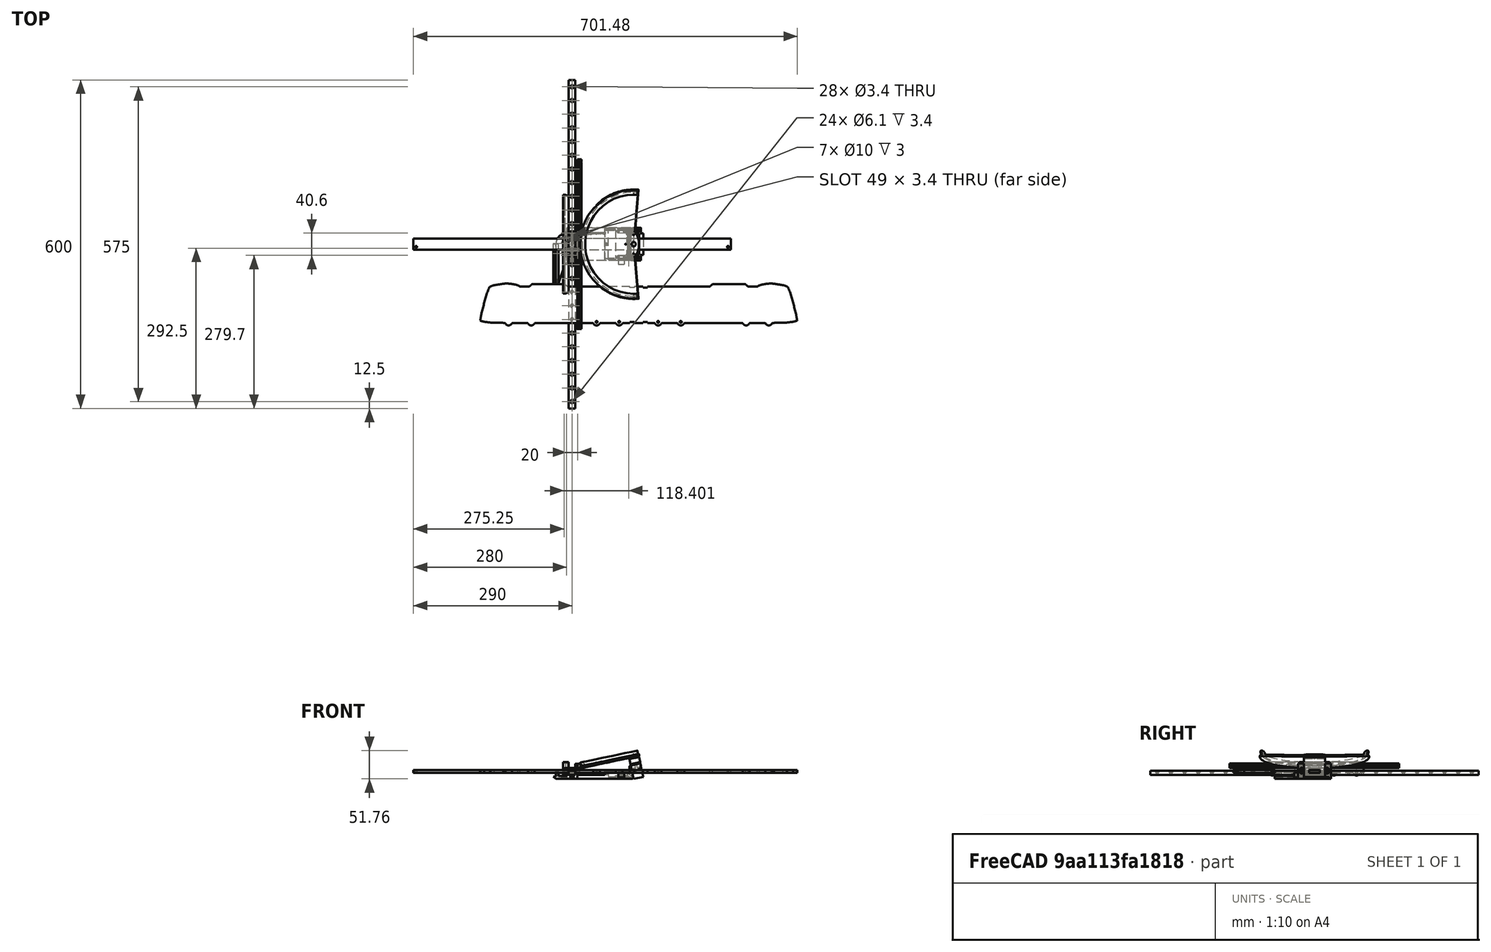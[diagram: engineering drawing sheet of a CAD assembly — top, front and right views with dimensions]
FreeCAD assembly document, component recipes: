
FREECAD ASSEMBLY — COMPONENT RECIPES ("mechanism")

This assembly document has 15 components, labeled P0..P14 below (a component is one placed body or linked part). 14 of them carry a construction recipe — the FreeCAD feature program that regenerates the part from scratch, quoted from this document or its linked companion documents; the rest are supplied as boundary geometry only. No exploded tour is included for this assembly.
NOTE — document 2 of 2 of this assembly tour. The two overview renders and the header above are repeated from document 1; the component sections below continue where the previous document stopped.
COMPONENT P12 — recipe-attached ("Stand001", modeled in this document).
Construction recipe (the document's own serialized feature program — sketch geometry with constraints, then the solid features built on it; lengths are millimeters unless a unit is written):

FEATURE [PartDesign::SubShapeBinder] Binder012
  BindCopyOnChange = 0
  BindMode = 0
  ClaimChildren = false
  Context = -> Body006 [Binder012.]
  Fuse = false
  MakeFace = true
  OffsetFill = false
  OffsetIntersection = false
  OffsetJoinType = 0
  OffsetOpenResult = false
  PartialLoad = false
  Refine = true
  Relative = true
  Support = -> [Body002[Sketch006.]]
  _Version = 2
FEATURE [PartDesign::Pad] Pad008  label="StandFootPad"
  Direction = (0,1,0)
  Length = 60
  Length2 = 10
  Midplane = true
  Profile = -> Binder012
  Refine = true
  Suppressed = false
  Type = 0
FEATURE [PartDesign::Mirrored] Mirrored003
  BaseFeature = -> Pad008
  MirrorPlane = -> YZ_Plane006
  Originals = -> [Pad008]
  Refine = true
  Suppressed = false
  TransformMode = 0
FEATURE [PartDesign::SubShapeBinder] Binder013
  BindCopyOnChange = 0
  BindMode = 0
  ClaimChildren = false
  Context = -> Body006 [Binder013.]
  Fuse = false
  MakeFace = true
  OffsetFill = false
  OffsetIntersection = false
  OffsetJoinType = 0
  OffsetOpenResult = false
  PartialLoad = false
  Refine = true
  Relative = true
  Support = -> [Body005[Sketch019.]]
  _Version = 2
FEATURE [Sketcher::SketchObject] Sketch023  label="StandCrossSection"
  ArcFitTolerance = 1e-06
  AttachmentSupport = -> [XZ_Plane006]
  ExternalGeometry = -> [Mirrored003,Binder013]
  FullyConstrained = true
  MakeInternals = false
  MapMode = 5
  Placement = pos=(0,0,0) rot=(1,0,0;1.5708rad)
  expr: Constraints[18] = <<PinionCrossSection>>.Constraints.ServoBodyWidth
  expr: Constraints[8] = <<PinionCrossSection>>.Constraints.ServoShaftLength
  sketch-geometry (26):
    g0: LineSegment StartX=9.7 StartY=-11 StartZ=0 EndX=108.652 EndY=-11 EndZ=0
    g1: LineSegment StartX=59.8197 StartY=-4 StartZ=0 EndX=9.7 EndY=-4 EndZ=0
    g2: LineSegment StartX=9.7 StartY=-4 StartZ=0 EndX=9.7 EndY=-11 EndZ=0
    g3: LineSegment [constr] StartX=112.51 StartY=31.9532 StartZ=0 EndX=113.539 EndY=27.0602 EndZ=0
    g4: LineSegment [constr] StartX=104.732 StartY=25.2077 StartZ=0 EndX=122.347 EndY=28.9128 EndZ=0
    g5: LineSegment [constr] StartX=122.347 StartY=28.9128 StartZ=0 EndX=129.963 EndY=-7.29486 EndZ=0
    g6: LineSegment [constr] StartX=129.963 StartY=-7.29486 StartZ=0 EndX=112.348 EndY=-11 EndZ=0
    g7: LineSegment [constr] StartX=112.348 StartY=-11 StartZ=0 EndX=104.732 EndY=25.2077 EndZ=0
    g8: LineSegment [constr] StartX=106.688 StartY=15.9111 StartZ=0 EndX=124.302 EndY=19.6162 EndZ=0
    g9: LineSegment [constr] StartX=124.817 StartY=17.1698 StartZ=0 EndX=107.202 EndY=13.4646 EndZ=0
    g10: LineSegment StartX=107.202 StartY=13.4646 StartZ=0 EndX=124.817 EndY=17.1698 EndZ=0
    g11: LineSegment StartX=124.817 StartY=17.1698 StartZ=0 EndX=125.64 EndY=13.2554 EndZ=0
    g12: LineSegment StartX=123.187 StartY=7.04679 StartZ=0 EndX=112.054 EndY=-0.748697 EndZ=0
    g13: LineSegment StartX=110.839 StartY=-3.82368 StartZ=0 EndX=111.587 EndY=-7.38248 EndZ=0
    g14: ArcOfCircle CenterX=108.652 CenterY=-8 CenterZ=0 NormalX=0 NormalY=0 NormalZ=1 AngleXU=0 Radius=3 StartAngle=4.71239 EndAngle=6.49051
    g15: GeomPoint [constr] X=112.348 Y=-11 Z=0
    g16: ArcOfCircle CenterX=113.774 CenterY=-3.20615 CenterZ=0 NormalX=0 NormalY=0 NormalZ=1 AngleXU=0 Radius=3 StartAngle=2.18166 EndAngle=3.34892
    g17: GeomPoint [constr] X=110.431 Y=-1.88501 Z=0
    g18: ArcOfCircle CenterX=119.713 CenterY=12.0086 CenterZ=0 NormalX=0 NormalY=0 NormalZ=1 AngleXU=0 Radius=6.05726 StartAngle=5.32325 EndAngle=6.49051
    g19: GeomPoint [constr] X=126.463 Y=9.3411 Z=0
    g20: ArcOfCircle CenterX=107.82 CenterY=10.5289 CenterZ=0 NormalX=0 NormalY=0 NormalZ=1 AngleXU=0 Radius=3 StartAngle=1.77812 EndAngle=3.14159
    g21: LineSegment StartX=104.82 StartY=4 StartZ=0 EndX=61.8197 EndY=4 EndZ=0
    g22: LineSegment StartX=59.8197 StartY=-4 StartZ=0 EndX=59.8197 EndY=2 EndZ=0
    g23: ArcOfCircle CenterX=61.8197 CenterY=2 CenterZ=0 NormalX=0 NormalY=0 NormalZ=1 AngleXU=0 Radius=2 StartAngle=1.5708 EndAngle=3.14159
    g24: GeomPoint [constr] X=59.8197 Y=4 Z=0
    g25: LineSegment StartX=104.82 StartY=10.5289 StartZ=0 EndX=104.82 EndY=4 EndZ=0
  constraints (65):
    c: Coincident(g1,g2)
    c: Coincident(g2,g0)
    c: Horizontal(g0)
    c: Horizontal(g1)
    c: Coincident(g0,g-3)
    c: Coincident(g-3,g1)
    c: Coincident(g3,g-4)
    c: PointOnObject(g-4,g3)
    c: Distance(g3,g3) = 5
    c: Coincident(g4,g5)
    c: Coincident(g5,g6)
    c: Coincident(g6,g7)
    c: Coincident(g7,g4)
    c: Perpendicular(g4,g7)
    c: Perpendicular(g5,g4)
    c: Perpendicular(g6,g5)
    c: Parallel(g3,g7)
    c: Symmetric(g4,g4,g3)
    c: Distance(g6,g6) = 18
    c: PointOnObject(g8,g7)
    c: PointOnObject(g8,g5)
    c: PointOnObject(g9,g5)
    c: PointOnObject(g9,g7)
    c: Perpendicular(g8,g7)
    c: Perpendicular(g7,g9)
    c: Distance(g8,g9) = 2.5  'ServoFlangeThickness'
    c: Distance(g9,g5) = 25  'ServoUnderFlangeHeight'
    c: Coincident(g15,g6)
    c: Coincident(g10,g9)
    c: Coincident(g11,g9)
    c: PointOnObject(g19,g5)
    c: PointOnObject(g17,g7)
    c: Distance(g11,g19) = 8
    c: PointOnObject(g15,g0)
    c: PointOnObject(g15,g13)
    c: Tangent(g0,g14) = -1.5708
    c: Tangent(g13,g14) = 1.5708
    c: Radius(g14) = 3
    c: PointOnObject(g17,g13)
    c: PointOnObject(g17,g12)
    c: Tangent(g13,g16) = -1.5708
    c: Tangent(g12,g16) = -1.5708
    c: Radius(g16) = 3
    c: PointOnObject(g19,g12)
    c: Tangent(g11,g18) = 1.5708
    c: Tangent(g12,g18) = 1.5708
    c: Symmetric(g9,g19,g11)
    c: Horizontal(g21)
    c: Coincident(g22,g1)
    c: Vertical(g22)
    c: Coincident(g10,g9)
    c: Tangent(g20,g10) = 1.5708
    c: PointOnObject(g24,g22)
    c: PointOnObject(g24,g21)
    c: Tangent(g22,g23) = 1.5708
    c: Tangent(g21,g23) = -1.5708
    c: Radius(g23) = 2
    c: Distance(g24,g0) = 15
    c: Radius(g20) = 3
    c: Coincident(g25,g20)
    c: Coincident(g25,g21)
    c: Vertical(g25)
    c: DistanceX(g24,g21) = 45
    c: Horizontal(g20,g20)
    c: Angle(g12,g25) = 0.959931
FEATURE [PartDesign::Pad] Pad009
  BaseFeature = -> Mirrored003
  Direction = (0,-1,2e-16)
  Length = 60
  Length2 = 10
  Midplane = true
  Profile = -> Sketch023
  ReferenceAxis = -> Sketch023 [N_Axis]
  Refine = true
  Suppressed = false
  Type = 0
  expr: Length = <<StandFootPad>>.Length
FEATURE [Sketcher::SketchObject] Sketch024  label="ServoCutout"
  ArcFitTolerance = 1e-06
  AttachmentSupport = -> [Pad009]
  ExternalGeometry = -> [Pad009]
  FullyConstrained = true
  MakeInternals = false
  MapMode = 5
  Placement = pos=(1.83,-2e-15,-8.69996) rot=(0,-1,0;0.207323rad)
  sketch-geometry (4):
    g0: LineSegment StartX=107.678 StartY=19.5 StartZ=0 EndX=107.678 EndY=-19.5 EndZ=0
    g1: LineSegment StartX=107.678 StartY=-19.5 StartZ=0 EndX=125.678 EndY=-19.5 EndZ=0
    g2: LineSegment StartX=125.678 StartY=-19.5 StartZ=0 EndX=125.678 EndY=19.5 EndZ=0
    g3: LineSegment StartX=125.678 StartY=19.5 StartZ=0 EndX=107.678 EndY=19.5 EndZ=0
  constraints (11):
    c: Coincident(g0,g1)
    c: Coincident(g1,g2)
    c: Coincident(g2,g3)
    c: Coincident(g3,g0)
    c: Vertical(g0)
    c: Horizontal(g1)
    c: Horizontal(g3)
    c: PointOnObject(g0,g-3)
    c: PointOnObject(g1,g-4)
    c: DistanceY(g2,g2) = 39  'ServoDepth'
    c: Symmetric(g2,g1,g-1)
FEATURE [PartDesign::Pocket] Pocket006
  BaseFeature = -> Pad009
  Direction = (0.205841,0,-0.978585)
  Length = 5
  Length2 = 5
  Profile = -> Sketch024
  ReferenceAxis = -> Sketch024 [N_Axis]
  Refine = true
  Suppressed = false
  Type = 1
FEATURE [Sketcher::SketchObject] Sketch025
  ArcFitTolerance = 1e-06
  AttachmentSupport = -> [Pad009]
  ExternalGeometry = -> [Pad009]
  FullyConstrained = true
  MakeInternals = false
  MapMode = 5
  Placement = pos=(1.83,-2e-15,-8.69996) rot=(0,-1,0;0.207323rad)
  sketch-geometry (5):
    g0: LineSegment [constr] StartX=116.678 StartY=30 StartZ=0 EndX=116.678 EndY=-30 EndZ=0
    g1: Circle CenterX=111.678 CenterY=23.5 CenterZ=0 NormalX=0 NormalY=0 NormalZ=1 AngleXU=0 Radius=1.5
    g2: Circle CenterX=121.678 CenterY=23.5 CenterZ=0 NormalX=0 NormalY=0 NormalZ=1 AngleXU=0 Radius=1.5
    g3: Circle CenterX=111.678 CenterY=-23.5 CenterZ=0 NormalX=0 NormalY=0 NormalZ=1 AngleXU=0 Radius=1.5
    g4: Circle CenterX=121.678 CenterY=-23.5 CenterZ=0 NormalX=0 NormalY=0 NormalZ=1 AngleXU=0 Radius=1.5
  constraints (12):
    c: Vertical(g0)
    c: Symmetric(g-3,g-4,g0)
    c: Symmetric(g1,g2,g0)
    c: Symmetric(g3,g4,g0)
    c: Symmetric(g3,g1,g-1)
    c: DistanceY(g4,g2) = 47
    c: DistanceX(g1,g2) = 10
    c: Equal(g1,g2)
    c: Equal(g2,g4)
    c: Equal(g4,g3)
    c: Diameter(g1) = 3
    c: Horizontal(g0,g-4)
FEATURE [PartDesign::Hole] Hole005  label="ServoScrews"
  BaseFeature = -> Pocket006
  CustomThreadClearance = 0
  Depth = 303.612
  DepthType = 1
  Diameter = 5.5
  DrillForDepth = false
  DrillPoint = 1
  DrillPointAngle = 118
  HoleCutCountersinkAngle = 90
  HoleCutCustomValues = false
  HoleCutDepth = 6.5
  HoleCutDiameter = 6.5
  HoleCutType = 1
  ModelThread = false
  Profile = -> Sketch025
  Refine = true
  Suppressed = false
  Tapered = false
  TaperedAngle = 90
  ThreadClass = 0
  ThreadDepth = 303.612
  ThreadDepthType = 0
  ThreadDirection = 0
  ThreadFit = 0
  ThreadSize = 13
  ThreadType = 1
  Threaded = false
  UseCustomThreadClearance = false
FEATURE [Sketcher::SketchObject] Sketch026
  ArcFitTolerance = 1e-06
  AttachmentSupport = -> [XY_Plane006]
  FullyConstrained = true
  MakeInternals = false
  MapMode = 5
  sketch-geometry (1):
    g0: Circle CenterX=0 CenterY=0 CenterZ=0 NormalX=0 NormalY=0 NormalZ=1 AngleXU=0 Radius=1.5
  constraints (2):
    c: Diameter(g0) = 3
    c: Coincident(g0,g-1)
FEATURE [PartDesign::Hole] Hole006  label="Rail Screw"
  BaseFeature = -> Hole005
  CustomThreadClearance = 0
  Depth = 303.612
  DepthType = 1
  Diameter = 4.4
  DrillForDepth = false
  DrillPoint = 1
  DrillPointAngle = 118
  HoleCutCountersinkAngle = 90
  HoleCutCustomValues = false
  HoleCutDepth = 0
  HoleCutDiameter = 6.1
  HoleCutType = 0
  ModelThread = false
  Profile = -> Sketch026
  Refine = true
  Suppressed = false
  Tapered = false
  TaperedAngle = 90
  ThreadClass = 0
  ThreadDepth = 303.612
  ThreadDepthType = 0
  ThreadDirection = 0
  ThreadFit = 0
  ThreadSize = 0
  ThreadType = 0
  Threaded = false
  UseCustomThreadClearance = false
FEATURE [Sketcher::SketchObject] Sketch027
  ArcFitTolerance = 1e-06
  AttachmentSupport = -> [Hole006]
  ExternalGeometry = -> [Hole006]
  FullyConstrained = true
  MakeInternals = false
  MapMode = 5
  Placement = pos=(0,0,-11) rot=(1,0,0;3.14159rad)
  expr: Constraints[23] = <<FootPads>>.Constraints.FootDiameter
  sketch-geometry (11):
    g0: LineSegment [constr] StartX=0 StartY=20.3 StartZ=0 EndX=0 EndY=-20.3 EndZ=0
    g1: LineSegment [constr] StartX=0 StartY=-20.3 StartZ=0 EndX=103.652 EndY=-20.3 EndZ=0
    g2: LineSegment [constr] StartX=103.652 StartY=-20.3 StartZ=0 EndX=103.652 EndY=20.3 EndZ=0
    g3: LineSegment [constr] StartX=103.652 StartY=20.3 StartZ=0 EndX=0 EndY=20.3 EndZ=0
    g4: LineSegment [constr] StartX=0 StartY=20.3 StartZ=0 EndX=-9.7 EndY=20.3 EndZ=0
    g5: LineSegment [constr] StartX=0 StartY=20.3 StartZ=0 EndX=0 EndY=30 EndZ=0
    g6: Circle CenterX=0 CenterY=20.3 CenterZ=0 NormalX=0 NormalY=0 NormalZ=1 AngleXU=0 Radius=5
    g7: Circle CenterX=103.652 CenterY=20.3 CenterZ=0 NormalX=0 NormalY=0 NormalZ=1 AngleXU=0 Radius=5
    g8: Circle CenterX=103.652 CenterY=-20.3 CenterZ=0 NormalX=0 NormalY=0 NormalZ=1 AngleXU=0 Radius=5
    g9: Circle CenterX=0 CenterY=-20.3 CenterZ=0 NormalX=0 NormalY=0 NormalZ=1 AngleXU=0 Radius=5
    g10: GeomPoint [constr] X=108.652 Y=20.3 Z=0
  constraints (27):
    c: Coincident(g0,g1)
    c: Coincident(g1,g2)
    c: Coincident(g2,g3)
    c: Coincident(g3,g0)
    c: Vertical(g0)
    c: Horizontal(g1)
    c: Horizontal(g3)
    c: Symmetric(g2,g1,g-1)
    c: PointOnObject(g-1,g0)
    c: Coincident(g4,g0)
    c: PointOnObject(g4,g-3)
    c: Horizontal(g4)
    c: Coincident(g5,g0)
    c: PointOnObject(g5,g-2)
    c: Horizontal(g-3,g5)
    c: Equal(g4,g5)
    c: Coincident(g6,g0)
    c: Coincident(g7,g2)
    c: Coincident(g8,g1)
    c: Coincident(g9,g0)
    c: Equal(g9,g8)
    c: Equal(g8,g7)
    c: Equal(g7,g6)
    c: Diameter(g6) = 10
    c: PointOnObject(g10,g7)
    c: Horizontal(g2,g10)
    c: PointOnObject(g10,g-4)
FEATURE [PartDesign::Pocket] Pocket007  label="FootPads001"
  BaseFeature = -> Hole006
  Direction = (0,0,1)
  Length = 3
  Length2 = 5
  Profile = -> Sketch027
  ReferenceAxis = -> Sketch027 [N_Axis]
  Refine = true
  Suppressed = false
  Type = 0
  expr: Length = <<FootPadPocket>>.Length
FEATURE [PartDesign::SubShapeBinder] Binder016
  BindCopyOnChange = 0
  BindMode = 0
  ClaimChildren = false
  Context = -> Body006 [Binder016.]
  Fuse = false
  MakeFace = true
  OffsetFill = false
  OffsetIntersection = false
  OffsetJoinType = 0
  OffsetOpenResult = false
  PartialLoad = false
  Refine = true
  Relative = true
  Support = -> [Body008[Pad016.Face4]]
  _Version = 2
FEATURE [Sketcher::SketchObject] Sketch037
  ArcFitTolerance = 1e-06
  AttachmentSupport = -> [Pocket007]
  ExternalGeometry = -> [Binder016,Pocket007]
  FullyConstrained = true
  MakeInternals = false
  MapMode = 5
  Placement = pos=(0,9e-16,4) rot=(0,0,1;0rad)
  sketch-geometry (6):
    g0: LineSegment StartX=65.8197 StartY=26 StartZ=0 EndX=65.8197 EndY=-26 EndZ=0
    g1: LineSegment StartX=65.8197 StartY=-26 StartZ=0 EndX=100.82 EndY=-26 EndZ=0
    g2: LineSegment StartX=100.82 StartY=-26 StartZ=0 EndX=100.82 EndY=26 EndZ=0
    g3: LineSegment StartX=100.82 StartY=26 StartZ=0 EndX=65.8197 EndY=26 EndZ=0
    g4: LineSegment [constr] StartX=65.8197 StartY=-26 StartZ=0 EndX=61.8197 EndY=-26 EndZ=0
    g5: LineSegment [constr] StartX=100.82 StartY=-26 StartZ=0 EndX=104.82 EndY=-26 EndZ=0
  constraints (17):
    c: Coincident(g0,g1)
    c: Coincident(g1,g2)
    c: Coincident(g2,g3)
    c: Coincident(g3,g0)
    c: Vertical(g2)
    c: Horizontal(g1)
    c: Horizontal(g3)
    c: Symmetric(g0,g0,g-1)
    c: Distance(g1,g-4) = 0.5
    c: Coincident(g4,g0)
    c: Horizontal(g4)
    c: Coincident(g5,g1)
    c: Horizontal(g5)
    c: Vertical(g5,g-6)
    c: Vertical(g4,g-5)
    c: Equal(g4,g5)
    c: Distance(g-5,g0) = 4
FEATURE [PartDesign::Pocket] Pocket011  label="ElectronicsCarveOut"
  BaseFeature = -> Pocket007
  Direction = (0,0,-1)
  Length = 0
  Length2 = 5
  Offset = 1
  Profile = -> Sketch037
  ReferenceAxis = -> Sketch037 [N_Axis]
  Refine = true
  Suppressed = false
  Type = 3
  UpToFace = -> Binder016 [Face1]
FEATURE [Sketcher::SketchObject] Sketch038
  ArcFitTolerance = 1e-06
  AttachmentSupport = -> [Pocket011]
  ExternalGeometry = -> [Binder016]
  FullyConstrained = true
  MakeInternals = false
  MapMode = 5
  Placement = pos=(0,0,-7) rot=(0,0,1;0rad)
  sketch-geometry (6):
    g0: Circle CenterX=84.3 CenterY=23.5 CenterZ=0 NormalX=0 NormalY=0 NormalZ=1 AngleXU=0 Radius=2.35
    g1: Circle CenterX=95.7 CenterY=23.5 CenterZ=0 NormalX=0 NormalY=0 NormalZ=1 AngleXU=0 Radius=2.35
    g2: Circle CenterX=84.3 CenterY=-23.5 CenterZ=0 NormalX=0 NormalY=0 NormalZ=1 AngleXU=0 Radius=2.35
    g3: Circle CenterX=95.7 CenterY=-23.5 CenterZ=0 NormalX=0 NormalY=0 NormalZ=1 AngleXU=0 Radius=2.35
    g4: GeomPoint X=84.3 Y=24.55 Z=0
    g5: GeomPoint X=84.3 Y=25.85 Z=0
  constraints (12):
    c: Coincident(g0,g-3)
    c: Coincident(g1,g-4)
    c: Coincident(g2,g-5)
    c: Coincident(g3,g-6)
    c: Equal(g2,g3)
    c: Equal(g3,g0)
    c: Equal(g0,g1)
    c: PointOnObject(g4,g-3)
    c: PointOnObject(g5,g0)
    c: Vertical(g0,g4)
    c: Vertical(g4,g5)
    c: Distance(g4,g0) = 1.3
FEATURE [PartDesign::Pad] Pad017  label="PCBStandoff"
  BaseFeature = -> Pocket011
  Direction = (0,0,1)
  Length = 10
  Length2 = 10
  Profile = -> Sketch038
  ReferenceAxis = -> Sketch038 [N_Axis]
  Refine = true
  Suppressed = false
  Type = 3
  UpToFace = -> Binder016 [Face1]
FEATURE [Sketcher::SketchObject] Sketch039
  ArcFitTolerance = 1e-06
  AttachmentSupport = -> [Pad017]
  ExternalGeometry = -> [Binder016]
  FullyConstrained = true
  MakeInternals = false
  MapMode = 5
  Placement = pos=(0,0,-6) rot=(0,0,1;0rad)
  sketch-geometry (4):
    g0: Circle CenterX=84.3 CenterY=23.5 CenterZ=0 NormalX=0 NormalY=0 NormalZ=1 AngleXU=0 Radius=1.05
    g1: Circle CenterX=95.7 CenterY=23.5 CenterZ=0 NormalX=0 NormalY=0 NormalZ=1 AngleXU=0 Radius=1.05
    g2: Circle CenterX=84.3 CenterY=-23.5 CenterZ=0 NormalX=0 NormalY=0 NormalZ=1 AngleXU=0 Radius=1.05
    g3: Circle CenterX=95.7 CenterY=-23.5 CenterZ=0 NormalX=0 NormalY=0 NormalZ=1 AngleXU=0 Radius=1.05
  constraints (8):
    c: Coincident(g0,g-3)
    c: Equal(g0,g-3)
    c: Coincident(g1,g-4)
    c: Equal(g1,g-4)
    c: Coincident(g2,g-5)
    c: Equal(g2,g-5)
    c: Coincident(g3,g-6)
    c: Equal(g3,g-6)
FEATURE [PartDesign::Hole] Hole007  label="PCBMountHoles"
  BaseFeature = -> Pad017
  CustomThreadClearance = 0
  Depth = 3.5
  DepthType = 0
  Diameter = 3
  DrillForDepth = false
  DrillPoint = 0
  DrillPointAngle = 118
  HoleCutCountersinkAngle = 90
  HoleCutCustomValues = false
  HoleCutDepth = 0
  HoleCutDiameter = 6.1
  HoleCutType = 0
  ModelThread = false
  Profile = -> Sketch039
  Refine = true
  Suppressed = false
  Tapered = false
  TaperedAngle = 90
  ThreadClass = 0
  ThreadDepth = 3.5
  ThreadDepthType = 0
  ThreadDirection = 0
  ThreadFit = 0
  ThreadSize = 0
  ThreadType = 0
  Threaded = false
  UseCustomThreadClearance = false
FEATURE [PartDesign::SubShapeBinder] Binder017
  BindCopyOnChange = 0
  BindMode = 0
  ClaimChildren = false
  Context = -> Body006 [Binder017.]
  Fuse = false
  MakeFace = true
  OffsetFill = false
  OffsetIntersection = false
  OffsetJoinType = 0
  OffsetOpenResult = false
  PartialLoad = false
  Refine = true
  Relative = true
  Support = -> [Body008[Pad016.Face14,Pad016.Face15,Pad016.Face16]]
  _Version = 2
FEATURE [Sketcher::SketchObject] Sketch040
  ArcFitTolerance = 1e-06
  AttachmentSupport = -> [Hole007]
  ExternalGeometry = -> [Binder017]
  FullyConstrained = true
  MakeInternals = false
  MapMode = 5
  Placement = pos=(0,-30,8.1e-15) rot=(1,0,0;1.5708rad)
  sketch-geometry (10):
    g0: LineSegment StartX=84.5 StartY=-0.3 StartZ=0 EndX=84.5 EndY=-7.3 EndZ=0
    g1: LineSegment StartX=85.5 StartY=-8.3 StartZ=0 EndX=94.5 EndY=-8.3 EndZ=0
    g2: LineSegment StartX=95.5 StartY=-7.3 StartZ=0 EndX=95.5 EndY=-0.3 EndZ=0
    g3: LineSegment StartX=94.5 StartY=0.7 StartZ=0 EndX=85.5 EndY=0.7 EndZ=0
    g4: ArcOfCircle CenterX=85.5 CenterY=-0.3 CenterZ=0 NormalX=0 NormalY=0 NormalZ=1 AngleXU=0 Radius=1 StartAngle=1.5708 EndAngle=3.14159
    g5: ArcOfCircle CenterX=85.5 CenterY=-7.3 CenterZ=0 NormalX=0 NormalY=0 NormalZ=1 AngleXU=0 Radius=1 StartAngle=3.14159 EndAngle=4.71239
    g6: ArcOfCircle CenterX=94.5 CenterY=-7.3 CenterZ=0 NormalX=0 NormalY=0 NormalZ=1 AngleXU=0 Radius=1 StartAngle=4.71239 EndAngle=6.28319
    g7: ArcOfCircle CenterX=94.5 CenterY=-0.3 CenterZ=0 NormalX=0 NormalY=0 NormalZ=1 AngleXU=0 Radius=1 StartAngle=0 EndAngle=1.5708
    g8: GeomPoint [constr] X=84.5 Y=0.7 Z=0
    g9: GeomPoint [constr] X=95.5 Y=-8.3 Z=0
  constraints (22):
    c: Tangent(g0,g4) = -1.5708
    c: Tangent(g0,g5) = -1.5708
    c: Tangent(g1,g5) = -1.5708
    c: Tangent(g1,g6) = -1.5708
    c: Tangent(g2,g6) = -1.5708
    c: Tangent(g2,g7) = -1.5708
    c: Tangent(g3,g7) = -1.5708
    c: Tangent(g3,g4) = -1.5708
    c: Vertical(g0)
    c: Vertical(g2)
    c: Horizontal(g1)
    c: Horizontal(g3)
    c: Equal(g4,g5)
    c: Equal(g5,g6)
    c: Equal(g6,g7)
    c: PointOnObject(g8,g0)
    c: PointOnObject(g8,g3)
    c: PointOnObject(g9,g1)
    c: PointOnObject(g9,g2)
    c: Radius(g5) = 1
    c: Coincident(g8,g-3)
    c: Coincident(g9,g-4)
FEATURE [PartDesign::Pocket] Pocket012  label="USBPlugCarve"
  BaseFeature = -> Hole007
  Direction = (0,1,-2e-16)
  Length = 0
  Length2 = 5
  Profile = -> Sketch040
  ReferenceAxis = -> Sketch040 [N_Axis]
  Refine = true
  Suppressed = false
  Type = 3
  UpToFace = -> Binder017 [Face3]
FEATURE [Sketcher::SketchObject] Sketch041
  ArcFitTolerance = 1e-06
  AttachmentSupport = -> [Pocket012]
  ExternalGeometry = -> [Binder017]
  FullyConstrained = true
  MakeInternals = false
  MapMode = 5
  Placement = pos=(0,-26.8,0) rot=(1,0,0;1.5708rad)
  sketch-geometry (12):
    g0: LineSegment [constr] StartX=86 StartY=-2.3 StartZ=0 EndX=86 EndY=-5.3 EndZ=0
    g1: LineSegment [constr] StartX=86 StartY=-5.3 StartZ=0 EndX=94 EndY=-5.3 EndZ=0
    g2: LineSegment [constr] StartX=94 StartY=-5.3 StartZ=0 EndX=94 EndY=-2.3 EndZ=0
    g3: LineSegment [constr] StartX=94 StartY=-2.3 StartZ=0 EndX=86 EndY=-2.3 EndZ=0
    g4: LineSegment StartX=94.3 StartY=-5.3 StartZ=0 EndX=94.3 EndY=-2.3 EndZ=0
    g5: ArcOfCircle CenterX=94 CenterY=-2.3 CenterZ=0 NormalX=0 NormalY=0 NormalZ=-1 AngleXU=0 Radius=0.3 StartAngle=1.5708 EndAngle=3.14159
    g6: LineSegment StartX=94 StartY=-2 StartZ=0 EndX=86 EndY=-2 EndZ=0
    g7: ArcOfCircle CenterX=86 CenterY=-2.3 CenterZ=0 NormalX=0 NormalY=0 NormalZ=-1 AngleXU=-1.5708 Radius=0.3 StartAngle=1.5708 EndAngle=3.14159
    g8: LineSegment StartX=85.7 StartY=-2.3 StartZ=0 EndX=85.7 EndY=-5.3 EndZ=0
    g9: ArcOfCircle CenterX=86 CenterY=-5.3 CenterZ=0 NormalX=0 NormalY=0 NormalZ=-1 AngleXU=-3.14159 Radius=0.3 StartAngle=1.5708 EndAngle=3.14159
    g10: LineSegment StartX=86 StartY=-5.6 StartZ=0 EndX=94 EndY=-5.6 EndZ=0
    g11: ArcOfCircle CenterX=94 CenterY=-5.3 CenterZ=0 NormalX=0 NormalY=0 NormalZ=-1 AngleXU=1.5708 Radius=0.3 StartAngle=1.5708 EndAngle=3.14159
  constraints (26):
    c: Coincident(g0,g1)
    c: Coincident(g1,g2)
    c: Coincident(g2,g3)
    c: Coincident(g3,g0)
    c: Vertical(g0)
    c: Vertical(g2)
    c: Horizontal(g1)
    c: Horizontal(g3)
    c: Coincident(g0,g-3)
    c: Coincident(g1,g-4)
    c: Tangent(g4,g5) = -1.5708
    c: Tangent(g4,g11) = -1.5708
    c: Tangent(g5,g6) = -1.5708
    c: Tangent(g6,g7) = -1.5708
    c: Tangent(g7,g8) = -1.5708
    c: Tangent(g8,g9) = -1.5708
    c: Tangent(g9,g10) = -1.5708
    c: Tangent(g10,g11) = -1.5708
    c: Coincident(g11,g1)
    c: Parallel(g4,g2)
    c: Coincident(g5,g3)
    c: Parallel(g6,g3)
    c: Coincident(g7,g3)
    c: Parallel(g8,g0)
    c: Coincident(g9,g0)
    c: Distance(g10,g1) = 0.3
FEATURE [PartDesign::Pocket] Pocket013  label="USBSocketCarve"
  BaseFeature = -> Pocket012
  Direction = (0,1,-2e-16)
  Length = 5
  Length2 = 5
  Profile = -> Sketch041
  ReferenceAxis = -> Sketch041 [N_Axis]
  Refine = true
  Suppressed = false
  Type = 2
FEATURE [Sketcher::SketchObject] Sketch042
  ArcFitTolerance = 1e-06
  AttachmentSupport = -> [Pocket013]
  ExternalGeometry = -> [Pocket013]
  FullyConstrained = true
  MakeInternals = false
  MapMode = 5
  Placement = pos=(100.82,0,0) rot=(0.57735,-0.57735,-0.57735;2.0944rad)
  sketch-geometry (4):
    g0: LineSegment StartX=-26 StartY=4 StartZ=0 EndX=-28 EndY=2 EndZ=0
    g1: LineSegment StartX=-28 StartY=2 StartZ=0 EndX=28 EndY=2 EndZ=0
    g2: LineSegment StartX=28 StartY=2 StartZ=0 EndX=26 EndY=4 EndZ=0
    g3: LineSegment StartX=26 StartY=4 StartZ=0 EndX=-26 EndY=4 EndZ=0
  constraints (11):
    c: Distance(g-6,g-3) = 2
    c: Coincident(g0,g-5)
    c: PointOnObject(g0,g-6)
    c: Coincident(g0,g1)
    c: PointOnObject(g1,g-6)
    c: Coincident(g1,g2)
    c: Coincident(g2,g-4)
    c: Coincident(g2,g3)
    c: Coincident(g3,g0)
    c: Angle(g1,g0) = 0.785398
    c: Equal(g0,g2)
FEATURE [PartDesign::Pocket] Pocket014  label="LidSlot"
  BaseFeature = -> Pocket013
  Direction = (1,0,0)
  Length = 0
  Length2 = 5
  Profile = -> Sketch042
  ReferenceAxis = -> Sketch042 [N_Axis]
  Refine = true
  Suppressed = false
  Type = 3
  UpToFace = -> Pocket013 [Face17]
FEATURE [PartDesign::Pocket] Pocket015  label="LidOvershoot"
  BaseFeature = -> Pocket014
  Direction = (1,0,0)
  Length = 2
  Length2 = 5
  Profile = -> Sketch042
  ReferenceAxis = -> Sketch042 [N_Axis]
  Refine = true
  Suppressed = false
  Type = 0
FEATURE [Sketcher::SketchObject] Sketch043
  ArcFitTolerance = 1e-06
  AttachmentSupport = -> [Pocket015]
  ExternalGeometry = -> [Pocket015]
  FullyConstrained = true
  MakeInternals = false
  MapMode = 5
  Placement = pos=(0,0,2) rot=(0,0,1;0rad)
  sketch-geometry (3):
    g0: Circle CenterX=62.8197 CenterY=-1.9806e-12 CenterZ=0 NormalX=0 NormalY=0 NormalZ=1 AngleXU=0 Radius=1.5
    g1: GeomPoint X=59.8197 Y=-3.9648e-12 Z=0
    g2: GeomPoint X=65.8197 Y=3.6e-15 Z=0
  constraints (4):
    c: Symmetric(g-4,g-4,g1)
    c: Symmetric(g-3,g-3,g2)
    c: Symmetric(g1,g2,g0)
    c: Diameter(g0) = 3
FEATURE [PartDesign::Hole] Hole008  label="LidScrewHole"
  BaseFeature = -> Pocket015
  CustomThreadClearance = 0
  Depth = 6
  DepthType = 0
  Diameter = 3
  DrillForDepth = false
  DrillPoint = 0
  DrillPointAngle = 118
  HoleCutCountersinkAngle = 90
  HoleCutCustomValues = false
  HoleCutDepth = 0
  HoleCutDiameter = 6.1
  HoleCutType = 0
  ModelThread = false
  Profile = -> Sketch043
  Refine = true
  Suppressed = false
  Tapered = false
  TaperedAngle = 90
  ThreadClass = 0
  ThreadDepth = 6
  ThreadDepthType = 0
  ThreadDirection = 0
  ThreadFit = 0
  ThreadSize = 0
  ThreadType = 0
  Threaded = false
  UseCustomThreadClearance = false
FEATURE [Sketcher::SketchObject] Sketch044  label="SocketPipeSection"
  ArcFitTolerance = 1e-06
  AttachmentSupport = -> [Hole008]
  ExternalGeometry = -> [Hole008]
  FullyConstrained = true
  MakeInternals = false
  MapMode = 5
  Placement = pos=(100.82,0,0) rot=(0.57735,-0.57735,-0.57735;2.0944rad)
  expr: Constraints[10] = 7.62 + 2
  expr: Constraints[11] = 2.54 + 2
  sketch-geometry (4):
    g0: LineSegment StartX=-26 StartY=-4.54 StartZ=0 EndX=-16.38 EndY=-4.54 EndZ=0
    g1: LineSegment StartX=-16.38 StartY=-4.54 StartZ=0 EndX=-16.38 EndY=0 EndZ=0
    g2: LineSegment StartX=-16.38 StartY=0 StartZ=0 EndX=-26 EndY=0 EndZ=0
    g3: LineSegment StartX=-26 StartY=0 StartZ=0 EndX=-26 EndY=-4.54 EndZ=0
  constraints (12):
    c: Coincident(g0,g1)
    c: Coincident(g1,g2)
    c: Coincident(g2,g3)
    c: Coincident(g3,g0)
    c: Horizontal(g0)
    c: Horizontal(g2)
    c: Vertical(g1)
    c: Vertical(g3)
    c: PointOnObject(g0,g-4)
    c: PointOnObject(g1,g-1)
    c: DistanceX(g0,g0) = 9.62
    c: Distance(g1,g1) = 4.54
FEATURE [Sketcher::SketchObject] Sketch045  label="SocketPipePath"
  ArcFitTolerance = 1e-06
  AttachmentSupport = -> [Hole008]
  ExternalGeometry = -> [Sketch044,Hole008]
  FullyConstrained = true
  MakeInternals = false
  MapMode = 5
  Placement = pos=(0,26,0) rot=(1,0,0;1.5708rad)
  sketch-geometry (2):
    g0: LineSegment StartX=100.82 StartY=-1.9e-15 StartZ=0 EndX=111.652 EndY=-7.42652 EndZ=0
    g1: GeomPoint [constr] X=111.652 Y=-8 Z=0
  constraints (5):
    c: Coincident(g0,g-3)
    c: PointOnObject(g1,g-5)
    c: Horizontal(g-5,g1)
    c: PointOnObject(g-5,g0)
    c: Vertical(g0,g1)
FEATURE [PartDesign::SubtractivePipe] SubtractivePipe  label="ServoCablePipe"
  AuxilleryCurvelinear = true
  AuxillerySpineTangent = false
  BaseFeature = -> Hole008
  Binormal = (0,0,0)
  Mode = 0
  Profile = -> Sketch044
  Refine = true
  Spine = -> Sketch045
  SpineTangent = false
  Suppressed = false
  Transformation = 0
  Transition = 0
FEATURE [Sketcher::SketchObject] Sketch049
  ArcFitTolerance = 1e-06
  AttachmentSupport = -> [XZ_Plane006]
  ExternalGeometry = -> [SubtractivePipe]
  FullyConstrained = true
  MakeInternals = false
  MapMode = 5
  Placement = pos=(0,0,0) rot=(1,0,0;1.5708rad)
  sketch-geometry (3):
    g0: LineSegment StartX=101.665 StartY=4 StartZ=0 EndX=102.82 EndY=2 EndZ=0
    g1: LineSegment StartX=102.82 StartY=2 StartZ=0 EndX=102.82 EndY=4 EndZ=0
    g2: LineSegment StartX=102.82 StartY=4 StartZ=0 EndX=101.665 EndY=4 EndZ=0
  constraints (7):
    c: Coincident(g0,g1)
    c: Coincident(g1,g2)
    c: Coincident(g2,g0)
    c: Horizontal(g2)
    c: Angle(g0,g-1) = 1.0472
    c: Coincident(g1,g-3)
    c: Coincident(g0,g-3)
FEATURE [PartDesign::Pad] Pad020  label="LidRearLip"
  BaseFeature = -> SubtractivePipe
  Direction = (0,-1,2e-16)
  Length = 10
  Length2 = 10
  Profile = -> Sketch049
  ReferenceAxis = -> Sketch049 [N_Axis]
  Refine = true
  Suppressed = false
  Type = 2
FEATURE [PartDesign::Mirrored] Mirrored004  label="LidRearLipReflection"
  BaseFeature = -> Pad020
  MirrorPlane = -> XZ_Plane006
  Originals = -> [Pad020]
  Refine = true
  Suppressed = false
  TransformMode = 0
FEATURE [Sketcher::SketchObject] Sketch065
  ArcFitTolerance = 1e-06
  FullyConstrained = false
  MakeInternals = false
  Placement = pos=(0,0,-11) rot=(0,0,-1;3.14159rad)
  sketch-geometry (193):
    g0: LineSegment StartX=-17 StartY=-18.5371 StartZ=0 EndX=-17 EndY=-21.5 EndZ=0
    g1: LineSegment StartX=-17 StartY=-21.5 StartZ=0 EndX=-17.7681 EndY=-21.5 EndZ=0
    g2: LineSegment StartX=-17.7681 StartY=-21.5 StartZ=0 EndX=-17.7681 EndY=-19.7222 EndZ=0
    g3: BSplineCurve PolesCount=4 KnotsCount=2 Degree=3 IsPeriodic=0
    g4: BSplineCurve PolesCount=4 KnotsCount=2 Degree=3 IsPeriodic=0
    g5: LineSegment StartX=-18.7119 StartY=-19.5246 StartZ=0 EndX=-18.7119 EndY=-21.5 EndZ=0
    g6: LineSegment StartX=-18.7119 StartY=-21.5 StartZ=0 EndX=-19.4801 EndY=-21.5 EndZ=0
    g7: LineSegment StartX=-19.4801 StartY=-21.5 StartZ=0 EndX=-19.4801 EndY=-19.7222 EndZ=0
    g8: BSplineCurve PolesCount=4 KnotsCount=2 Degree=3 IsPeriodic=0
    g9: BSplineCurve PolesCount=4 KnotsCount=2 Degree=3 IsPeriodic=0
    g10: LineSegment StartX=-20.424 StartY=-19.5246 StartZ=0 EndX=-20.424 EndY=-21.5 EndZ=0
    g11: LineSegment StartX=-20.424 StartY=-21.5 StartZ=0 EndX=-21.1922 EndY=-21.5 EndZ=0
    g12: LineSegment StartX=-21.1922 StartY=-21.5 StartZ=0 EndX=-21.1922 EndY=-19.4041 EndZ=0
    g13: BSplineCurve PolesCount=4 KnotsCount=2 Degree=3 IsPeriodic=0
    g14: BSplineCurve PolesCount=4 KnotsCount=2 Degree=3 IsPeriodic=0
    g15: BSplineCurve PolesCount=4 KnotsCount=2 Degree=3 IsPeriodic=0
    g16: BSplineCurve PolesCount=4 KnotsCount=2 Degree=3 IsPeriodic=0
    g17: LineSegment StartX=-17.7627 StartY=-18.9047 StartZ=0 EndX=-17.7627 EndY=-18.5371 EndZ=0
    g18: LineSegment StartX=-17.7627 StartY=-18.5371 StartZ=0 EndX=-17 EndY=-18.5371 EndZ=0
    g19: BSplineCurve PolesCount=4 KnotsCount=2 Degree=3 IsPeriodic=0
    g20: BSplineCurve PolesCount=4 KnotsCount=2 Degree=3 IsPeriodic=0
    g21: LineSegment StartX=-23.536 StartY=-21.5 StartZ=0 EndX=-24.3702 EndY=-21.5 EndZ=0
    g22: LineSegment StartX=-24.3702 StartY=-21.5 StartZ=0 EndX=-24.3702 EndY=-21.4068 EndZ=0
    g23: BSplineCurve PolesCount=4 KnotsCount=2 Degree=3 IsPeriodic=0
    g24: LineSegment StartX=-24.1946 StartY=-21.0447 StartZ=0 EndX=-24.1946 EndY=-19.3985 EndZ=0
    g25: BSplineCurve PolesCount=4 KnotsCount=2 Degree=3 IsPeriodic=0
    g26: BSplineCurve PolesCount=4 KnotsCount=2 Degree=3 IsPeriodic=0
    g27: LineSegment StartX=-21.7143 StartY=-19.5138 StartZ=0 EndX=-22.455 EndY=-19.5138 EndZ=0
    g28: BSplineCurve PolesCount=4 KnotsCount=2 Degree=3 IsPeriodic=0
    g29: BSplineCurve PolesCount=4 KnotsCount=2 Degree=3 IsPeriodic=0
    g30: BSplineCurve PolesCount=4 KnotsCount=2 Degree=3 IsPeriodic=0
    g31: LineSegment StartX=-22.8282 StartY=-19.7497 StartZ=0 EndX=-22.5209 EndY=-19.8045 EndZ=0
    g32: BSplineCurve PolesCount=4 KnotsCount=2 Degree=3 IsPeriodic=0
    g33: BSplineCurve PolesCount=4 KnotsCount=2 Degree=3 IsPeriodic=0
    g34: BSplineCurve PolesCount=4 KnotsCount=2 Degree=3 IsPeriodic=0
    g35: BSplineCurve PolesCount=4 KnotsCount=2 Degree=3 IsPeriodic=0
    g36: BSplineCurve PolesCount=4 KnotsCount=2 Degree=3 IsPeriodic=0
    g37: LineSegment StartX=-22.8557 StartY=-20.2436 StartZ=0 EndX=-23.1191 EndY=-20.1941 EndZ=0
    g38: BSplineCurve PolesCount=4 KnotsCount=2 Degree=3 IsPeriodic=0
    g39: LineSegment StartX=-23.4428 StartY=-20.1009 StartZ=0 EndX=-23.4428 EndY=-20.3093 EndZ=0
    g40: LineSegment StartX=-25.6028 StartY=-18.5371 StartZ=0 EndX=-24.8348 EndY=-18.5371 EndZ=0
    g41: LineSegment StartX=-24.8348 StartY=-18.5371 StartZ=0 EndX=-24.8348 EndY=-21.5 EndZ=0
    g42: LineSegment StartX=-24.8348 StartY=-21.5 StartZ=0 EndX=-25.6028 EndY=-21.5 EndZ=0
    g43: LineSegment StartX=-25.6028 StartY=-21.5 StartZ=0 EndX=-25.6028 EndY=-18.5371 EndZ=0
    g44: LineSegment StartX=-25.6028 StartY=-17.5 StartZ=0 EndX=-24.8348 EndY=-17.5 EndZ=0
    g45: LineSegment StartX=-24.8348 StartY=-17.5 StartZ=0 EndX=-24.8348 EndY=-18.1859 EndZ=0
    g46: LineSegment StartX=-24.8348 StartY=-18.1859 StartZ=0 EndX=-25.6028 EndY=-18.1859 EndZ=0
    g47: LineSegment StartX=-25.6028 StartY=-18.1859 StartZ=0 EndX=-25.6028 EndY=-17.5 EndZ=0
    g48: LineSegment StartX=-27.0432 StartY=-17.5 StartZ=0 EndX=-26.2752 EndY=-17.5 EndZ=0
    g49: LineSegment StartX=-26.2752 StartY=-17.5 StartZ=0 EndX=-26.2752 EndY=-21.5 EndZ=0
    g50: LineSegment StartX=-26.2752 StartY=-21.5 StartZ=0 EndX=-27.0432 EndY=-21.5 EndZ=0
    g51: LineSegment StartX=-27.0432 StartY=-21.5 StartZ=0 EndX=-27.0432 EndY=-17.5 EndZ=0
    g52: BSplineCurve PolesCount=4 KnotsCount=2 Degree=3 IsPeriodic=0
    g53: BSplineCurve PolesCount=4 KnotsCount=2 Degree=3 IsPeriodic=0
    g54: BSplineCurve PolesCount=4 KnotsCount=2 Degree=3 IsPeriodic=0
    g55: BSplineCurve PolesCount=4 KnotsCount=2 Degree=3 IsPeriodic=0
    g56: BSplineCurve PolesCount=4 KnotsCount=2 Degree=3 IsPeriodic=0
    g57: BSplineCurve PolesCount=4 KnotsCount=2 Degree=3 IsPeriodic=0
    g58: BSplineCurve PolesCount=4 KnotsCount=2 Degree=3 IsPeriodic=0
    g59: BSplineCurve PolesCount=4 KnotsCount=2 Degree=3 IsPeriodic=0
    g60: BSplineCurve PolesCount=4 KnotsCount=2 Degree=3 IsPeriodic=0
    g61: LineSegment StartX=-31.384 StartY=-22.005 StartZ=0 EndX=-31.2304 EndY=-21.6043 EndZ=0
    g62: BSplineCurve PolesCount=4 KnotsCount=2 Degree=3 IsPeriodic=0
    g63: BSplineCurve PolesCount=4 KnotsCount=2 Degree=3 IsPeriodic=0
    g64: BSplineCurve PolesCount=4 KnotsCount=2 Degree=3 IsPeriodic=0
    g65: BSplineCurve PolesCount=4 KnotsCount=2 Degree=3 IsPeriodic=0
    g66: BSplineCurve PolesCount=4 KnotsCount=2 Degree=3 IsPeriodic=0
    g67: BSplineCurve PolesCount=4 KnotsCount=2 Degree=3 IsPeriodic=0
    g68: BSplineCurve PolesCount=4 KnotsCount=2 Degree=3 IsPeriodic=0
    g69: BSplineCurve PolesCount=4 KnotsCount=2 Degree=3 IsPeriodic=0
    g70: LineSegment StartX=-31.0275 StartY=-20.249 StartZ=0 EndX=-31.4555 EndY=-18.7126 EndZ=0
    g71: LineSegment StartX=-31.4555 StartY=-18.7126 StartZ=0 EndX=-30.9616 EndY=-18.7126 EndZ=0
    g72: LineSegment StartX=-30.9616 StartY=-18.7126 StartZ=0 EndX=-30.8737 EndY=-19.0529 EndZ=0
    g73: BSplineCurve PolesCount=4 KnotsCount=2 Degree=3 IsPeriodic=0
    g74: BSplineCurve PolesCount=4 KnotsCount=2 Degree=3 IsPeriodic=0
    g75: BSplineCurve PolesCount=4 KnotsCount=2 Degree=3 IsPeriodic=0
    g76: BSplineCurve PolesCount=4 KnotsCount=2 Degree=3 IsPeriodic=0
    g77: BSplineCurve PolesCount=4 KnotsCount=2 Degree=3 IsPeriodic=0
    g78: BSplineCurve PolesCount=4 KnotsCount=2 Degree=3 IsPeriodic=0
    g79: LineSegment StartX=-33.9302 StartY=-18.5371 StartZ=0 EndX=-33.162 EndY=-18.5371 EndZ=0
    g80: LineSegment StartX=-33.162 StartY=-18.5371 StartZ=0 EndX=-33.162 EndY=-21.8458 EndZ=0
    g81: BSplineCurve PolesCount=4 KnotsCount=2 Degree=3 IsPeriodic=0
    g82: BSplineCurve PolesCount=4 KnotsCount=2 Degree=3 IsPeriodic=0
    g83: LineSegment StartX=-32.7998 StartY=-22.0543 StartZ=0 EndX=-32.7998 EndY=-22.6689 EndZ=0
    g84: BSplineCurve PolesCount=4 KnotsCount=2 Degree=3 IsPeriodic=0
    g85: BSplineCurve PolesCount=4 KnotsCount=2 Degree=3 IsPeriodic=0
    g86: LineSegment StartX=-33.9302 StartY=-22.0159 StartZ=0 EndX=-33.9302 EndY=-18.5371 EndZ=0
    g87: LineSegment StartX=-33.9302 StartY=-17.5 StartZ=0 EndX=-33.162 EndY=-17.5 EndZ=0
    g88: LineSegment StartX=-33.162 StartY=-17.5 StartZ=0 EndX=-33.162 EndY=-18.1859 EndZ=0
    g89: LineSegment StartX=-33.162 StartY=-18.1859 StartZ=0 EndX=-33.9302 EndY=-18.1859 EndZ=0
    g90: LineSegment StartX=-33.9302 StartY=-18.1859 StartZ=0 EndX=-33.9302 EndY=-17.5 EndZ=0
    g91: LineSegment StartX=-36.3843 StartY=-19.6893 StartZ=0 EndX=-36.3843 EndY=-21.5 EndZ=0
    g92: LineSegment StartX=-36.3843 StartY=-21.5 StartZ=0 EndX=-37.1525 EndY=-21.5 EndZ=0
    g93: LineSegment StartX=-37.1525 StartY=-21.5 StartZ=0 EndX=-37.1525 EndY=-19.5138 EndZ=0
    g94: BSplineCurve PolesCount=4 KnotsCount=2 Degree=3 IsPeriodic=0
    g95: BSplineCurve PolesCount=4 KnotsCount=2 Degree=3 IsPeriodic=0
    g96: LineSegment StartX=-35.3197 StartY=-18.965 StartZ=0 EndX=-35.3197 EndY=-17.5 EndZ=0
    g97: LineSegment StartX=-35.3197 StartY=-17.5 StartZ=0 EndX=-34.5517 EndY=-17.5 EndZ=0
    g98: LineSegment StartX=-34.5517 StartY=-17.5 StartZ=0 EndX=-34.5517 EndY=-21.5 EndZ=0
    g99: LineSegment StartX=-34.5517 StartY=-21.5 StartZ=0 EndX=-35.3197 EndY=-21.5 EndZ=0
    g100: LineSegment StartX=-35.3197 StartY=-21.5 StartZ=0 EndX=-35.3197 EndY=-19.7222 EndZ=0
    g101: BSplineCurve PolesCount=4 KnotsCount=2 Degree=3 IsPeriodic=0
    g102: BSplineCurve PolesCount=4 KnotsCount=2 Degree=3 IsPeriodic=0
    g103: LineSegment StartX=-37.742 StartY=-18.5371 StartZ=0 EndX=-37.742 EndY=-21.5 EndZ=0
    g104: LineSegment StartX=-37.742 StartY=-21.5 StartZ=0 EndX=-38.5102 EndY=-21.5 EndZ=0
    g105: LineSegment StartX=-38.5102 StartY=-21.5 StartZ=0 EndX=-38.5102 EndY=-19.7222 EndZ=0
    g106: BSplineCurve PolesCount=4 KnotsCount=2 Degree=3 IsPeriodic=0
    g107: BSplineCurve PolesCount=4 KnotsCount=2 Degree=3 IsPeriodic=0
    g108: LineSegment StartX=-39.6241 StartY=-19.6729 StartZ=0 EndX=-39.6241 EndY=-21.5 EndZ=0
    g109: LineSegment StartX=-39.6241 StartY=-21.5 StartZ=0 EndX=-40.3922 EndY=-21.5 EndZ=0
    g110: LineSegment StartX=-40.3922 StartY=-21.5 StartZ=0 EndX=-40.3922 EndY=-19.5138 EndZ=0
    g111: BSplineCurve PolesCount=4 KnotsCount=2 Degree=3 IsPeriodic=0
    g112: BSplineCurve PolesCount=4 KnotsCount=2 Degree=3 IsPeriodic=0
    g113: LineSegment StartX=-38.5102 StartY=-18.965 StartZ=0 EndX=-38.5102 EndY=-18.5371 EndZ=0
    g114: LineSegment StartX=-38.5102 StartY=-18.5371 StartZ=0 EndX=-37.742 EndY=-18.5371 EndZ=0
    g115: BSplineCurve PolesCount=4 KnotsCount=2 Degree=3 IsPeriodic=0
    g116: BSplineCurve PolesCount=4 KnotsCount=2 Degree=3 IsPeriodic=0
    g117: BSplineCurve PolesCount=4 KnotsCount=2 Degree=3 IsPeriodic=0
    g118: LineSegment StartX=-43.5707 StartY=-20.666 StartZ=0 EndX=-42.8135 EndY=-20.666 EndZ=0
    g119: BSplineCurve PolesCount=4 KnotsCount=2 Degree=3 IsPeriodic=0
    g120: BSplineCurve PolesCount=4 KnotsCount=2 Degree=3 IsPeriodic=0
    g121: LineSegment StartX=-41.6118 StartY=-20.26 StartZ=0 EndX=-43.5982 EndY=-20.26 EndZ=0
    g122: BSplineCurve PolesCount=4 KnotsCount=2 Degree=3 IsPeriodic=0
    g123: BSplineCurve PolesCount=4 KnotsCount=2 Degree=3 IsPeriodic=0
    g124: LineSegment StartX=-42.8024 StartY=-19.7497 StartZ=0 EndX=-41.6228 EndY=-19.7497 EndZ=0
    g125: BSplineCurve PolesCount=4 KnotsCount=2 Degree=3 IsPeriodic=0
    g126: BSplineCurve PolesCount=4 KnotsCount=2 Degree=3 IsPeriodic=0
    g127: LineSegment StartX=-45.4039 StartY=-18.5974 StartZ=0 EndX=-44.9759 EndY=-18.5974 EndZ=0
    g128: LineSegment StartX=-44.9759 StartY=-18.5974 StartZ=0 EndX=-44.9759 EndY=-17.8017 EndZ=0
    g129: LineSegment StartX=-44.9759 StartY=-17.8017 StartZ=0 EndX=-44.2076 EndY=-17.8017 EndZ=0
    g130: LineSegment StartX=-44.2076 StartY=-17.8017 StartZ=0 EndX=-44.2076 EndY=-18.5974 EndZ=0
    g131: LineSegment StartX=-44.2076 StartY=-18.5974 StartZ=0 EndX=-43.8292 EndY=-18.5974 EndZ=0
    g132: LineSegment StartX=-43.8292 StartY=-18.5974 StartZ=0 EndX=-43.8292 EndY=-19.1078 EndZ=0
    g133: LineSegment StartX=-43.8292 StartY=-19.1078 StartZ=0 EndX=-44.2076 EndY=-19.1078 EndZ=0
    g134: LineSegment StartX=-44.2076 StartY=-19.1078 StartZ=0 EndX=-44.2076 EndY=-20.9295 EndZ=0
    g135: BSplineCurve PolesCount=4 KnotsCount=2 Degree=3 IsPeriodic=0
    g136: BSplineCurve PolesCount=4 KnotsCount=2 Degree=3 IsPeriodic=0
    g137: LineSegment StartX=-45.4039 StartY=-21.5659 StartZ=0 EndX=-45.4039 EndY=-21.0283 EndZ=0
    g138: BSplineCurve PolesCount=4 KnotsCount=2 Degree=3 IsPeriodic=0
    g139: BSplineCurve PolesCount=4 KnotsCount=2 Degree=3 IsPeriodic=0
    g140: LineSegment StartX=-44.9759 StartY=-20.7209 StartZ=0 EndX=-44.9759 EndY=-19.1078 EndZ=0
    g141: LineSegment StartX=-44.9759 StartY=-19.1078 StartZ=0 EndX=-45.4039 EndY=-19.1078 EndZ=0
    g142: LineSegment StartX=-45.4039 StartY=-19.1078 StartZ=0 EndX=-45.4039 EndY=-18.5974 EndZ=0
    g143: LineSegment StartX=-46.7556 StartY=-20.6989 StartZ=0 EndX=-45.9326 EndY=-20.6989 EndZ=0
    g144: LineSegment StartX=-45.9326 StartY=-20.6989 StartZ=0 EndX=-45.9326 EndY=-21.5 EndZ=0
    g145: LineSegment StartX=-45.9326 StartY=-21.5 StartZ=0 EndX=-46.7556 EndY=-21.5 EndZ=0
    g146: LineSegment StartX=-46.7556 StartY=-21.5 StartZ=0 EndX=-46.7556 EndY=-20.6989 EndZ=0
    g147: BSplineCurve PolesCount=4 KnotsCount=2 Degree=3 IsPeriodic=0
    g148: LineSegment StartX=-49.2308 StartY=-19.6454 StartZ=0 EndX=-49.966 EndY=-19.6454 EndZ=0
    g149: BSplineCurve PolesCount=4 KnotsCount=2 Degree=3 IsPeriodic=0
    g150: BSplineCurve PolesCount=4 KnotsCount=2 Degree=3 IsPeriodic=0
    g151: BSplineCurve PolesCount=4 KnotsCount=2 Degree=3 IsPeriodic=0
    g152: BSplineCurve PolesCount=4 KnotsCount=2 Degree=3 IsPeriodic=0
    g153: LineSegment StartX=-49.966 StartY=-20.474 StartZ=0 EndX=-49.2308 EndY=-20.474 EndZ=0
    g154: BSplineCurve PolesCount=4 KnotsCount=2 Degree=3 IsPeriodic=0
    g155: BSplineCurve PolesCount=4 KnotsCount=2 Degree=3 IsPeriodic=0
    g156: BSplineCurve PolesCount=4 KnotsCount=2 Degree=3 IsPeriodic=0
    g157: BSplineCurve PolesCount=4 KnotsCount=2 Degree=3 IsPeriodic=0
    g158: BSplineCurve PolesCount=4 KnotsCount=2 Degree=3 IsPeriodic=0
    g159: BSplineCurve PolesCount=4 KnotsCount=2 Degree=3 IsPeriodic=0
    g160: BSplineCurve PolesCount=4 KnotsCount=2 Degree=3 IsPeriodic=0
    g161: BSplineCurve PolesCount=4 KnotsCount=2 Degree=3 IsPeriodic=0
    g162: BSplineCurve PolesCount=4 KnotsCount=2 Degree=3 IsPeriodic=0
    g163: BSplineCurve PolesCount=4 KnotsCount=2 Degree=3 IsPeriodic=0
    g164: BSplineCurve PolesCount=4 KnotsCount=2 Degree=3 IsPeriodic=0
    g165: LineSegment StartX=-54.5406 StartY=-20.6989 StartZ=0 EndX=-53.7175 EndY=-20.6989 EndZ=0
    g166: LineSegment StartX=-53.7175 StartY=-20.6989 StartZ=0 EndX=-53.7175 EndY=-21.5 EndZ=0
    g167: LineSegment StartX=-53.7175 StartY=-21.5 StartZ=0 EndX=-54.5406 EndY=-21.5 EndZ=0
    g168: LineSegment StartX=-54.5406 StartY=-21.5 StartZ=0 EndX=-54.5406 EndY=-20.6989 EndZ=0
    g169: LineSegment StartX=-57.8552 StartY=-21.5 StartZ=0 EndX=-57.8552 EndY=-18.5371 EndZ=0
    g170: LineSegment StartX=-57.8552 StartY=-18.5371 StartZ=0 EndX=-57.087 EndY=-18.5371 EndZ=0
    g171: LineSegment StartX=-57.087 StartY=-18.5371 StartZ=0 EndX=-57.087 EndY=-20.3917 EndZ=0
    g172: BSplineCurve PolesCount=4 KnotsCount=2 Degree=3 IsPeriodic=0
    g173: BSplineCurve PolesCount=4 KnotsCount=2 Degree=3 IsPeriodic=0
    g174: LineSegment StartX=-55.9731 StartY=-20.4411 StartZ=0 EndX=-55.9731 EndY=-18.5371 EndZ=0
    g175: LineSegment StartX=-55.9731 StartY=-18.5371 StartZ=0 EndX=-55.2049 EndY=-18.5371 EndZ=0
    g176: LineSegment StartX=-55.2049 StartY=-18.5371 StartZ=0 EndX=-55.2049 EndY=-20.6001 EndZ=0
    g177: BSplineCurve PolesCount=4 KnotsCount=2 Degree=3 IsPeriodic=0
    g178: BSplineCurve PolesCount=4 KnotsCount=2 Degree=3 IsPeriodic=0
    g179: LineSegment StartX=-57.087 StartY=-21.1488 StartZ=0 EndX=-57.087 EndY=-21.5 EndZ=0
    g180: LineSegment StartX=-57.087 StartY=-21.5 StartZ=0 EndX=-57.8552 EndY=-21.5 EndZ=0
    g181: LineSegment StartX=-59.3281 StartY=-19.6893 StartZ=0 EndX=-59.3281 EndY=-17.5 EndZ=0
    g182: LineSegment StartX=-59.3281 StartY=-17.5 StartZ=0 EndX=-58.5599 EndY=-17.5 EndZ=0
    g183: LineSegment StartX=-58.5599 StartY=-17.5 StartZ=0 EndX=-58.5599 EndY=-21.5 EndZ=0
    g184: LineSegment StartX=-58.5599 StartY=-21.5 StartZ=0 EndX=-59.3281 EndY=-21.5 EndZ=0
    g185: LineSegment StartX=-59.3281 StartY=-21.5 StartZ=0 EndX=-59.3281 EndY=-20.5288 EndZ=0
    g186: LineSegment StartX=-59.3281 StartY=-20.5288 StartZ=0 EndX=-59.6353 EndY=-20.1941 EndZ=0
    g187: LineSegment StartX=-59.6353 StartY=-20.1941 StartZ=0 EndX=-60.3432 EndY=-21.5 EndZ=0
    g188: LineSegment StartX=-60.3432 StartY=-21.5 StartZ=0 EndX=-61.2431 EndY=-21.5 EndZ=0
    g189: LineSegment StartX=-61.2431 StartY=-21.5 StartZ=0 EndX=-60.1621 EndY=-19.6565 EndZ=0
    g190: LineSegment StartX=-60.1621 StartY=-19.6565 StartZ=0 EndX=-61.1718 EndY=-18.5371 EndZ=0
    g191: LineSegment StartX=-61.1718 StartY=-18.5371 StartZ=0 EndX=-60.2993 EndY=-18.5371 EndZ=0
    g192: LineSegment StartX=-60.2993 StartY=-18.5371 StartZ=0 EndX=-59.3281 EndY=-19.6893 EndZ=0
  constraints (286):
    c: Vertical(g0)
    c: Coincident(g0,g1)
    c: Horizontal(g1)
    c: Coincident(g1,g2)
    c: Vertical(g2)
    c: Coincident(g2,g3)
    c: Coincident(g3,g4)
    c: Coincident(g4,g5)
    c: Vertical(g5)
    c: Coincident(g5,g6)
    c: Horizontal(g6)
    c: Coincident(g6,g7)
    c: Vertical(g7)
    c: Coincident(g7,g8)
    c: Coincident(g8,g9)
    c: Coincident(g9,g10)
    c: Vertical(g10)
    c: Coincident(g10,g11)
    c: Horizontal(g11)
    c: Coincident(g11,g12)
    c: Vertical(g12)
    c: Coincident(g12,g13)
    c: Coincident(g13,g14)
    c: Coincident(g14,g15)
    c: Coincident(g15,g16)
    c: Coincident(g16,g17)
    c: Vertical(g17)
    c: Coincident(g17,g18)
    c: Horizontal(g18)
    c: Coincident(g18,g0)
    c: Coincident(g19,g20)
    c: Coincident(g20,g21)
    c: Horizontal(g21)
    c: Coincident(g21,g22)
    c: Vertical(g22)
    c: Coincident(g22,g23)
    c: Coincident(g23,g24)
    c: Vertical(g24)
    c: Coincident(g24,g25)
    c: Coincident(g25,g26)
    c: Coincident(g26,g27)
    c: Horizontal(g27)
    c: Coincident(g27,g28)
    c: Coincident(g28,g29)
    c: Coincident(g29,g30)
    c: Coincident(g30,g31)
    c: Coincident(g31,g32)
    c: Coincident(g32,g33)
    c: Coincident(g33,g19)
    c: Coincident(g34,g35)
    c: Coincident(g35,g36)
    c: Coincident(g36,g37)
    c: Coincident(g37,g38)
    c: Coincident(g38,g39)
    c: Vertical(g39)
    c: Coincident(g39,g34)
    c: Horizontal(g40)
    c: Coincident(g40,g41)
    c: Vertical(g41)
    c: Coincident(g41,g42)
    c: Horizontal(g42)
    c: Coincident(g42,g43)
    c: Vertical(g43)
    c: Coincident(g43,g40)
    c: Horizontal(g44)
    c: Coincident(g44,g45)
    c: Vertical(g45)
    c: Coincident(g45,g46)
    c: Horizontal(g46)
    c: Coincident(g46,g47)
    c: Vertical(g47)
    c: Coincident(g47,g44)
    c: Horizontal(g48)
    c: Coincident(g48,g49)
    c: Vertical(g49)
    c: Coincident(g49,g50)
    c: Horizontal(g50)
    c: Coincident(g50,g51)
    c: Vertical(g51)
    c: Coincident(g51,g48)
    c: Coincident(g52,g53)
    c: Coincident(g53,g54)
    c: Coincident(g54,g55)
    c: Coincident(g55,g56)
    c: Coincident(g56,g57)
    c: Coincident(g57,g58)
    c: Coincident(g58,g59)
    c: Coincident(g59,g60)
    c: Coincident(g60,g61)
    c: Coincident(g61,g62)
    c: Coincident(g62,g63)
    c: Coincident(g63,g64)
    c: Coincident(g64,g65)
    c: Coincident(g65,g66)
    c: Coincident(g66,g67)
    c: Coincident(g67,g68)
    c: Coincident(g68,g69)
    c: Coincident(g69,g70)
    c: Coincident(g70,g71)
    c: Horizontal(g71)
    c: Coincident(g71,g72)
    c: Coincident(g72,g73)
    c: Coincident(g73,g74)
    c: Coincident(g74,g52)
    c: Coincident(g75,g76)
    c: Coincident(g76,g77)
    c: Coincident(g77,g78)
    c: Coincident(g78,g75)
    c: Horizontal(g79)
    c: Coincident(g79,g80)
    c: Vertical(g80)
    c: Coincident(g80,g81)
    c: Coincident(g81,g82)
    c: Coincident(g82,g83)
    c: Vertical(g83)
    c: Coincident(g83,g84)
    c: Coincident(g84,g85)
    c: Coincident(g85,g86)
    c: Vertical(g86)
    c: Coincident(g86,g79)
    c: Horizontal(g87)
    c: Coincident(g87,g88)
    c: Vertical(g88)
    c: Coincident(g88,g89)
    c: Horizontal(g89)
    c: Coincident(g89,g90)
    c: Vertical(g90)
    c: Coincident(g90,g87)
    c: Vertical(g91)
    c: Coincident(g91,g92)
    c: Horizontal(g92)
    c: Coincident(g92,g93)
    c: Vertical(g93)
    c: Coincident(g93,g94)
    c: Coincident(g94,g95)
    c: Coincident(g95,g96)
    c: Vertical(g96)
    c: Coincident(g96,g97)
    c: Horizontal(g97)
    c: Coincident(g97,g98)
    c: Vertical(g98)
    c: Coincident(g98,g99)
    c: Horizontal(g99)
    c: Coincident(g99,g100)
    c: Vertical(g100)
    c: Coincident(g100,g101)
    c: Coincident(g101,g102)
    c: Coincident(g102,g91)
    c: Vertical(g103)
    c: Coincident(g103,g104)
    c: Horizontal(g104)
    c: Coincident(g104,g105)
    c: Vertical(g105)
    c: Coincident(g105,g106)
    c: Coincident(g106,g107)
    c: Coincident(g107,g108)
    c: Vertical(g108)
    c: Coincident(g108,g109)
    c: Horizontal(g109)
    c: Coincident(g109,g110)
    c: Vertical(g110)
    c: Coincident(g110,g111)
    c: Coincident(g111,g112)
    c: Coincident(g112,g113)
    c: Vertical(g113)
    c: Coincident(g113,g114)
    c: Horizontal(g114)
    c: Coincident(g114,g103)
    c: Coincident(g115,g116)
    c: Coincident(g116,g117)
    c: Coincident(g117,g118)
    c: Horizontal(g118)
    c: Coincident(g118,g119)
    c: Coincident(g119,g120)
    c: Coincident(g120,g121)
    c: Horizontal(g121)
    c: Coincident(g121,g122)
    c: Coincident(g122,g123)
    c: Coincident(g123,g115)
    c: Horizontal(g124)
    c: Coincident(g124,g125)
    c: Coincident(g125,g126)
    c: Coincident(g126,g124)
    c: Horizontal(g127)
    c: Coincident(g127,g128)
    c: Vertical(g128)
    c: Coincident(g128,g129)
    c: Horizontal(g129)
    c: Coincident(g129,g130)
    c: Vertical(g130)
    c: Coincident(g130,g131)
    c: Horizontal(g131)
    c: Coincident(g131,g132)
    c: Vertical(g132)
    c: Coincident(g132,g133)
    c: Horizontal(g133)
    c: Coincident(g133,g134)
    c: Vertical(g134)
    c: Coincident(g134,g135)
    c: Coincident(g135,g136)
    c: Coincident(g136,g137)
    c: Vertical(g137)
    c: Coincident(g137,g138)
    c: Coincident(g138,g139)
    c: Coincident(g139,g140)
    c: Vertical(g140)
    c: Coincident(g140,g141)
    c: Horizontal(g141)
    c: Coincident(g141,g142)
    c: Vertical(g142)
    c: Coincident(g142,g127)
    c: Horizontal(g143)
    c: Coincident(g143,g144)
    c: Vertical(g144)
    c: Coincident(g144,g145)
    c: Horizontal(g145)
    c: Coincident(g145,g146)
    c: Vertical(g146)
    c: Coincident(g146,g143)
    c: Coincident(g147,g148)
    c: Horizontal(g148)
    c: Coincident(g148,g149)
    c: Coincident(g149,g150)
    c: Coincident(g150,g151)
    c: Coincident(g151,g152)
    c: Coincident(g152,g153)
    c: Horizontal(g153)
    c: Coincident(g153,g154)
    c: Coincident(g154,g155)
    c: Coincident(g155,g156)
    c: Coincident(g156,g147)
    c: Coincident(g157,g158)
    c: Coincident(g158,g159)
    c: Coincident(g159,g160)
    c: Coincident(g160,g157)
    c: Coincident(g161,g162)
    c: Coincident(g162,g163)
    c: Coincident(g163,g164)
    c: Coincident(g164,g161)
    c: Horizontal(g165)
    c: Coincident(g165,g166)
    c: Vertical(g166)
    c: Coincident(g166,g167)
    c: Horizontal(g167)
    c: Coincident(g167,g168)
    c: Vertical(g168)
    c: Coincident(g168,g165)
    c: Vertical(g169)
    c: Coincident(g169,g170)
    c: Horizontal(g170)
    c: Coincident(g170,g171)
    c: Vertical(g171)
    c: Coincident(g171,g172)
    c: Coincident(g172,g173)
    c: Coincident(g173,g174)
    c: Vertical(g174)
    c: Coincident(g174,g175)
    c: Horizontal(g175)
    c: Coincident(g175,g176)
    c: Vertical(g176)
    c: Coincident(g176,g177)
    c: Coincident(g177,g178)
    c: Coincident(g178,g179)
    c: Vertical(g179)
    c: Coincident(g179,g180)
    c: Horizontal(g180)
    c: Coincident(g180,g169)
    c: Vertical(g181)
    c: Coincident(g181,g182)
    c: Horizontal(g182)
    c: Coincident(g182,g183)
    c: Vertical(g183)
    c: Coincident(g183,g184)
    c: Horizontal(g184)
    c: Coincident(g184,g185)
    c: Vertical(g185)
    c: Coincident(g185,g186)
    c: Coincident(g186,g187)
    c: Coincident(g187,g188)
    c: Horizontal(g188)
    c: Coincident(g188,g189)
    c: Coincident(g189,g190)
    c: Coincident(g190,g191)
    c: Horizontal(g191)
    c: Coincident(g191,g192)
    c: Coincident(g192,g181)
FEATURE [PartDesign::Pocket] Pocket023
  BaseFeature = -> Mirrored004
  Direction = (0,0,-1)
  Length = 0.2
  Length2 = 5
  Profile = -> Sketch065
  ReferenceAxis = -> Sketch065 [N_Axis]
  Refine = true
  Reversed = true
  Suppressed = false
  Type = 0
FEATURE [PartDesign::Body] Body006  label="Stand"
  AllowCompound = false
  Group = -> [Binder012,Pad008,Mirrored003,Sketch023,Binder013,Pad009,Sketch024,Pocket006,Sketch025,Hole005,Sketch026,Hole006,Sketch027,Pocket007,Binder016,Sketch037,Pocket011,Sketch038,Pad017,Sketch039,Hole007,Binder017,Sketch040,Pocket012,Sketch041,Pocket013,Sketch042,Pocket014,Pocket015,Sketch043,Hole008,Sketch044,Sketch045,SubtractivePipe,Sketch049,Pad020,Mirrored004,Sketch065,Pocket023]
  Origin = -> Origin006
  Tip = -> Pocket023
COMPONENT P13 — recipe-attached ("TramCarriage001", modeled in this document).
Construction recipe (the document's own serialized feature program — sketch geometry with constraints, then the solid features built on it; lengths are millimeters unless a unit is written):

FEATURE [PartDesign::SubShapeBinder] Binder003
  BindCopyOnChange = 0
  BindMode = 0
  ClaimChildren = false
  Context = -> Body003 [Binder003.]
  Fuse = false
  MakeFace = true
  OffsetFill = false
  OffsetIntersection = false
  OffsetJoinType = 0
  OffsetOpenResult = false
  PartialLoad = false
  Refine = true
  Relative = true
  Support = -> [Body002[Sketch006.]]
  _Version = 2
FEATURE [PartDesign::SubShapeBinder] Binder004
  BindCopyOnChange = 0
  BindMode = 0
  ClaimChildren = false
  Context = -> Body003 [Binder004.]
  Fuse = false
  MakeFace = true
  OffsetFill = false
  OffsetIntersection = false
  OffsetJoinType = 0
  OffsetOpenResult = false
  PartialLoad = false
  Refine = true
  Relative = true
  Support = -> [Body001[Sketch001.]]
  _Version = 2
FEATURE [Sketcher::SketchObject] Sketch008
  ArcFitTolerance = 1e-06
  AttachmentSupport = -> [XZ_Plane003]
  ExternalGeometry = -> [Binder004,Binder003]
  FullyConstrained = true
  MakeInternals = false
  MapMode = 5
  Placement = pos=(0,0,0) rot=(1,0,0;1.5708rad)
  sketch-geometry (7):
    g0: LineSegment StartX=-6 StartY=9 StartZ=0 EndX=-13.5 EndY=9 EndZ=0
    g1: LineSegment StartX=-13.5 StartY=9 StartZ=0 EndX=-13.5 EndY=-6 EndZ=0
    g2: LineSegment StartX=-13.5 StartY=-6 StartZ=0 EndX=-16.5 EndY=-6 EndZ=0
    g3: LineSegment StartX=-16.5 StartY=-6 StartZ=0 EndX=-16.5 EndY=19.5 EndZ=0
    g4: LineSegment StartX=-16.5 StartY=19.5 StartZ=0 EndX=-6 EndY=19.5 EndZ=0
    g5: LineSegment StartX=-6 StartY=19.5 StartZ=0 EndX=-6 EndY=9 EndZ=0
    g6: LineSegment [constr] StartX=-11.25 StartY=19.5 StartZ=0 EndX=-11.25 EndY=7 EndZ=0
  constraints (21):
    c: PointOnObject(g0,g-4)
    c: Horizontal(g0)
    c: Coincident(g0,g1)
    c: PointOnObject(g1,g-6)
    c: Vertical(g1)
    c: Coincident(g1,g2)
    c: Horizontal(g2)
    c: Coincident(g2,g3)
    c: Vertical(g3)
    c: Coincident(g3,g4)
    c: Horizontal(g4)
    c: Coincident(g4,g5)
    c: Coincident(g5,g0)
    c: Vertical(g5)
    c: Distance(g2,g-5) = 5
    c: Distance(g2,g2) = 3
    c: PointOnObject(g0,g-7)
    c: Symmetric(g4,g4,g6)
    c: Vertical(g6)
    c: Distance(g6,g0) = 2
    c: DistanceY(g6,g6) = 12.5
FEATURE [PartDesign::Pad] Pad004
  Direction = (0,-1,2e-16)
  Length = 180
  Length2 = 10
  Midplane = true
  Placement = pos=(0,0,0) rot=(1,0,0;1.5708rad)
  Profile = -> Sketch008
  ReferenceAxis = -> Sketch008 [N_Axis]
  Refine = true
  Suppressed = false
  Type = 0
FEATURE [PartDesign::SubShapeBinder] Binder005
  BindCopyOnChange = 0
  BindMode = 0
  ClaimChildren = false
  Context = -> Body003 [Binder005.]
  Fuse = false
  MakeFace = true
  OffsetFill = false
  OffsetIntersection = false
  OffsetJoinType = 0
  OffsetOpenResult = false
  PartialLoad = false
  Refine = true
  Relative = true
  Support = -> [Body001[Pad002.Face14,Pad002.Face19]]
  _Version = 2
FEATURE [PartDesign::SubShapeBinder] Binder006
  BindCopyOnChange = 0
  BindMode = 0
  ClaimChildren = false
  Context = -> Body003 [Binder006.]
  Fuse = false
  MakeFace = true
  OffsetFill = false
  OffsetIntersection = false
  OffsetJoinType = 0
  OffsetOpenResult = false
  PartialLoad = false
  Refine = true
  Relative = true
  Support = -> [Body001[Sketch004.]]
  _Version = 2
FEATURE [Sketcher::SketchObject] Sketch010
  ArcFitTolerance = 1e-06
  AttachmentSupport = -> [Pad004]
  ExternalGeometry = -> [Binder006]
  FullyConstrained = true
  MakeInternals = false
  MapMode = 5
  Placement = pos=(0,8.6e-15,19.5) rot=(0,0,1;3.14159rad)
  sketch-geometry (2):
    g0: Circle CenterX=10 CenterY=-10 CenterZ=0 NormalX=0 NormalY=0 NormalZ=1 AngleXU=0 Radius=2.53403
    g1: Circle CenterX=10 CenterY=10 CenterZ=0 NormalX=0 NormalY=0 NormalZ=1 AngleXU=0 Radius=2.20024
  constraints (4):
    c: Coincident(g0,g-3)
    c: Equal(g0,g-3)
    c: Coincident(g1,g-4)
    c: Equal(g1,g-4)
FEATURE [PartDesign::Hole] Hole010
  BaseFeature = -> Pad004
  CustomThreadClearance = 0
  Depth = 367.842
  DepthType = 1
  Diameter = 3.4
  DrillForDepth = false
  DrillPoint = 1
  DrillPointAngle = 118
  HoleCutCountersinkAngle = 90
  HoleCutCustomValues = false
  HoleCutDepth = 2.5
  HoleCutDiameter = 6.1
  HoleCutType = 1
  ModelThread = false
  Placement = pos=(0,0,0) rot=(1,0,0;1.5708rad)
  Profile = -> Sketch010
  Refine = true
  Suppressed = false
  Tapered = false
  TaperedAngle = 90
  ThreadClass = 0
  ThreadDepth = 367.842
  ThreadDepthType = 0
  ThreadDirection = 0
  ThreadFit = 0
  ThreadSize = 9
  ThreadType = 1
  Threaded = false
  UseCustomThreadClearance = false
FEATURE [Sketcher::SketchObject] Sketch052  label="Tram"
  ArcFitTolerance = 1e-06
  AttachmentOffset = pos=(-3,0,0) rot=(0,0,1;1.5708rad)
  AttachmentSupport = -> [Hole010]
  FullyConstrained = false
  MakeInternals = false
  MapMode = 5
  Placement = pos=(-16.5,0,3) rot=(0.57735,-0.57735,-0.57735;2.0944rad)
  sketch-geometry (102):
    g0: BSplineCurve PolesCount=4 KnotsCount=2 Degree=3 IsPeriodic=0
    g1: BSplineCurve PolesCount=4 KnotsCount=2 Degree=3 IsPeriodic=0
    g2: BSplineCurve PolesCount=4 KnotsCount=2 Degree=3 IsPeriodic=0
    g3: BSplineCurve PolesCount=2 KnotsCount=2 Degree=1 IsPeriodic=0
    g4: BSplineCurve PolesCount=2 KnotsCount=2 Degree=1 IsPeriodic=0
    g5: BSplineCurve PolesCount=2 KnotsCount=2 Degree=1 IsPeriodic=0
    g6: BSplineCurve PolesCount=2 KnotsCount=2 Degree=1 IsPeriodic=0
    g7: BSplineCurve PolesCount=2 KnotsCount=2 Degree=1 IsPeriodic=0
    g8: BSplineCurve PolesCount=4 KnotsCount=2 Degree=3 IsPeriodic=0
    g9: BSplineCurve PolesCount=4 KnotsCount=2 Degree=3 IsPeriodic=0
    g10: BSplineCurve PolesCount=2 KnotsCount=2 Degree=1 IsPeriodic=0
    g11: BSplineCurve PolesCount=4 KnotsCount=2 Degree=3 IsPeriodic=0
    g12: BSplineCurve PolesCount=4 KnotsCount=2 Degree=3 IsPeriodic=0
    g13: BSplineCurve PolesCount=2 KnotsCount=2 Degree=1 IsPeriodic=0
    g14: BSplineCurve PolesCount=2 KnotsCount=2 Degree=1 IsPeriodic=0
    g15: BSplineCurve PolesCount=4 KnotsCount=2 Degree=3 IsPeriodic=0
    g16: BSplineCurve PolesCount=4 KnotsCount=2 Degree=3 IsPeriodic=0
    g17: BSplineCurve PolesCount=2 KnotsCount=2 Degree=1 IsPeriodic=0
    g18: BSplineCurve PolesCount=4 KnotsCount=2 Degree=3 IsPeriodic=0
    g19: BSplineCurve PolesCount=4 KnotsCount=2 Degree=3 IsPeriodic=0
    g20: BSplineCurve PolesCount=2 KnotsCount=2 Degree=1 IsPeriodic=0
    g21: BSplineCurve PolesCount=2 KnotsCount=2 Degree=1 IsPeriodic=0
    g22: BSplineCurve PolesCount=2 KnotsCount=2 Degree=1 IsPeriodic=0
    g23: BSplineCurve PolesCount=2 KnotsCount=2 Degree=1 IsPeriodic=0
    g24: BSplineCurve PolesCount=2 KnotsCount=2 Degree=1 IsPeriodic=0
    g25: BSplineCurve PolesCount=2 KnotsCount=2 Degree=1 IsPeriodic=0
    g26: BSplineCurve PolesCount=2 KnotsCount=2 Degree=1 IsPeriodic=0
    g27: BSplineCurve PolesCount=2 KnotsCount=2 Degree=1 IsPeriodic=0
    g28: BSplineCurve PolesCount=2 KnotsCount=2 Degree=1 IsPeriodic=0
    g29: BSplineCurve PolesCount=4 KnotsCount=2 Degree=3 IsPeriodic=0
    g30: BSplineCurve PolesCount=4 KnotsCount=2 Degree=3 IsPeriodic=0
    g31: BSplineCurve PolesCount=2 KnotsCount=2 Degree=1 IsPeriodic=0
    g32: BSplineCurve PolesCount=4 KnotsCount=2 Degree=3 IsPeriodic=0
    g33: BSplineCurve PolesCount=4 KnotsCount=2 Degree=3 IsPeriodic=0
    g34: BSplineCurve PolesCount=2 KnotsCount=2 Degree=1 IsPeriodic=0
    g35: BSplineCurve PolesCount=2 KnotsCount=2 Degree=1 IsPeriodic=0
    g36: BSplineCurve PolesCount=4 KnotsCount=2 Degree=3 IsPeriodic=0
    g37: BSplineCurve PolesCount=4 KnotsCount=2 Degree=3 IsPeriodic=0
    g38: BSplineCurve PolesCount=2 KnotsCount=2 Degree=1 IsPeriodic=0
    g39: BSplineCurve PolesCount=4 KnotsCount=2 Degree=3 IsPeriodic=0
    g40: BSplineCurve PolesCount=4 KnotsCount=2 Degree=3 IsPeriodic=0
    g41: BSplineCurve PolesCount=2 KnotsCount=2 Degree=1 IsPeriodic=0
    g42: BSplineCurve PolesCount=2 KnotsCount=2 Degree=1 IsPeriodic=0
    g43: BSplineCurve PolesCount=2 KnotsCount=2 Degree=1 IsPeriodic=0
    g44: BSplineCurve PolesCount=2 KnotsCount=2 Degree=1 IsPeriodic=0
    g45: BSplineCurve PolesCount=2 KnotsCount=2 Degree=1 IsPeriodic=0
    g46: BSplineCurve PolesCount=4 KnotsCount=2 Degree=3 IsPeriodic=0
    g47: BSplineCurve PolesCount=4 KnotsCount=2 Degree=3 IsPeriodic=0
    g48: BSplineCurve PolesCount=4 KnotsCount=2 Degree=3 IsPeriodic=0
    g49: BSplineCurve PolesCount=4 KnotsCount=2 Degree=3 IsPeriodic=0
    g50: BSplineCurve PolesCount=4 KnotsCount=2 Degree=3 IsPeriodic=0
    g51: BSplineCurve PolesCount=2 KnotsCount=2 Degree=1 IsPeriodic=0
    g52: BSplineCurve PolesCount=4 KnotsCount=2 Degree=3 IsPeriodic=0
    g53: BSplineCurve PolesCount=2 KnotsCount=2 Degree=1 IsPeriodic=0
    g54: BSplineCurve PolesCount=4 KnotsCount=2 Degree=3 IsPeriodic=0
    g55: BSplineCurve PolesCount=2 KnotsCount=2 Degree=1 IsPeriodic=0
    g56: BSplineCurve PolesCount=2 KnotsCount=2 Degree=1 IsPeriodic=0
    g57: BSplineCurve PolesCount=2 KnotsCount=2 Degree=1 IsPeriodic=0
    g58: BSplineCurve PolesCount=2 KnotsCount=2 Degree=1 IsPeriodic=0
    g59: BSplineCurve PolesCount=2 KnotsCount=2 Degree=1 IsPeriodic=0
    g60: BSplineCurve PolesCount=2 KnotsCount=2 Degree=1 IsPeriodic=0
    g61: BSplineCurve PolesCount=2 KnotsCount=2 Degree=1 IsPeriodic=0
    g62: BSplineCurve PolesCount=2 KnotsCount=2 Degree=1 IsPeriodic=0
    g63: BSplineCurve PolesCount=2 KnotsCount=2 Degree=1 IsPeriodic=0
    g64: BSplineCurve PolesCount=4 KnotsCount=2 Degree=3 IsPeriodic=0
    g65: BSplineCurve PolesCount=2 KnotsCount=2 Degree=1 IsPeriodic=0
    g66: BSplineCurve PolesCount=4 KnotsCount=2 Degree=3 IsPeriodic=0
    g67: BSplineCurve PolesCount=2 KnotsCount=2 Degree=1 IsPeriodic=0
    g68: BSplineCurve PolesCount=4 KnotsCount=2 Degree=3 IsPeriodic=0
    g69: BSplineCurve PolesCount=4 KnotsCount=2 Degree=3 IsPeriodic=0
    g70: BSplineCurve PolesCount=7 KnotsCount=4 Degree=2 IsPeriodic=0
    g71: BSplineCurve PolesCount=7 KnotsCount=4 Degree=2 IsPeriodic=0
    g72: BSplineCurve PolesCount=7 KnotsCount=4 Degree=2 IsPeriodic=0
    g73: BSplineCurve PolesCount=7 KnotsCount=4 Degree=2 IsPeriodic=0
    g74: BSplineCurve PolesCount=2 KnotsCount=2 Degree=1 IsPeriodic=0
    g75: BSplineCurve PolesCount=2 KnotsCount=2 Degree=1 IsPeriodic=0
    g76: BSplineCurve PolesCount=2 KnotsCount=2 Degree=1 IsPeriodic=0
    g77: BSplineCurve PolesCount=2 KnotsCount=2 Degree=1 IsPeriodic=0
    g78: BSplineCurve PolesCount=2 KnotsCount=2 Degree=1 IsPeriodic=0
    g79: BSplineCurve PolesCount=2 KnotsCount=2 Degree=1 IsPeriodic=0
    g80: BSplineCurve PolesCount=2 KnotsCount=2 Degree=1 IsPeriodic=0
    g81: BSplineCurve PolesCount=2 KnotsCount=2 Degree=1 IsPeriodic=0
    g82: BSplineCurve PolesCount=2 KnotsCount=2 Degree=1 IsPeriodic=0
    g83: BSplineCurve PolesCount=2 KnotsCount=2 Degree=1 IsPeriodic=0
    g84: BSplineCurve PolesCount=2 KnotsCount=2 Degree=1 IsPeriodic=0
    g85: BSplineCurve PolesCount=2 KnotsCount=2 Degree=1 IsPeriodic=0
    g86: BSplineCurve PolesCount=2 KnotsCount=2 Degree=1 IsPeriodic=0
    g87: BSplineCurve PolesCount=2 KnotsCount=2 Degree=1 IsPeriodic=0
    g88: BSplineCurve PolesCount=2 KnotsCount=2 Degree=1 IsPeriodic=0
    g89: BSplineCurve PolesCount=2 KnotsCount=2 Degree=1 IsPeriodic=0
    g90: BSplineCurve PolesCount=2 KnotsCount=2 Degree=1 IsPeriodic=0
    g91: BSplineCurve PolesCount=2 KnotsCount=2 Degree=1 IsPeriodic=0
    g92: BSplineCurve PolesCount=2 KnotsCount=2 Degree=1 IsPeriodic=0
    g93: BSplineCurve PolesCount=2 KnotsCount=2 Degree=1 IsPeriodic=0
    g94: BSplineCurve PolesCount=2 KnotsCount=2 Degree=1 IsPeriodic=0
    g95: BSplineCurve PolesCount=2 KnotsCount=2 Degree=1 IsPeriodic=0
    g96: BSplineCurve PolesCount=2 KnotsCount=2 Degree=1 IsPeriodic=0
    g97: BSplineCurve PolesCount=2 KnotsCount=2 Degree=1 IsPeriodic=0
    g98: BSplineCurve PolesCount=2 KnotsCount=2 Degree=1 IsPeriodic=0
    g99: BSplineCurve PolesCount=2 KnotsCount=2 Degree=1 IsPeriodic=0
    g100: BSplineCurve PolesCount=2 KnotsCount=2 Degree=1 IsPeriodic=0
    g101: BSplineCurve PolesCount=2 KnotsCount=2 Degree=1 IsPeriodic=0
  constraints (92):
    c: Coincident(g0,g1)
    c: Coincident(g1,g2)
    c: Coincident(g2,g3)
    c: Coincident(g3,g4)
    c: Coincident(g4,g5)
    c: Coincident(g5,g6)
    c: Coincident(g6,g7)
    c: Coincident(g7,g8)
    c: Coincident(g8,g9)
    c: Coincident(g9,g10)
    c: Coincident(g10,g11)
    c: Coincident(g11,g12)
    c: Coincident(g12,g13)
    c: Coincident(g13,g14)
    c: Coincident(g14,g15)
    c: Coincident(g15,g16)
    c: Coincident(g16,g17)
    c: Coincident(g17,g18)
    c: Coincident(g18,g19)
    c: Coincident(g19,g20)
    c: Coincident(g20,g21)
    c: Coincident(g21,g22)
    c: Coincident(g22,g23)
    c: Coincident(g23,g24)
    c: Coincident(g24,g25)
    c: Coincident(g25,g26)
    c: Coincident(g26,g27)
    c: Coincident(g27,g28)
    c: Coincident(g28,g29)
    c: Coincident(g29,g30)
    c: Coincident(g30,g31)
    c: Coincident(g31,g32)
    c: Coincident(g32,g33)
    c: Coincident(g33,g34)
    c: Coincident(g34,g35)
    c: Coincident(g35,g36)
    c: Coincident(g36,g37)
    c: Coincident(g37,g38)
    c: Coincident(g38,g39)
    c: Coincident(g39,g40)
    c: Coincident(g40,g41)
    c: Coincident(g41,g42)
    c: Coincident(g42,g43)
    c: Coincident(g43,g44)
    c: Coincident(g44,g45)
    c: Coincident(g45,g46)
    c: Coincident(g46,g47)
    c: Coincident(g47,g48)
    c: Coincident(g48,g49)
    c: Coincident(g49,g50)
    c: Coincident(g50,g51)
    c: Coincident(g51,g52)
    c: Coincident(g52,g53)
    c: Coincident(g53,g54)
    c: Coincident(g54,g55)
    c: Coincident(g55,g56)
    c: Coincident(g56,g57)
    c: Coincident(g57,g58)
    c: Coincident(g58,g59)
    c: Coincident(g59,g60)
    c: Coincident(g60,g61)
    c: Coincident(g61,g62)
    c: Coincident(g62,g63)
    c: Coincident(g63,g64)
    c: Coincident(g64,g65)
    c: Coincident(g65,g66)
    c: Coincident(g66,g67)
    c: Coincident(g67,g68)
    c: Coincident(g68,g69)
    c: Coincident(g69,g0)
    c: Coincident(g78,g79)
    c: Coincident(g79,g80)
    c: Coincident(g80,g81)
    c: Coincident(g81,g82)
    c: Coincident(g82,g83)
    c: Coincident(g83,g84)
    c: Coincident(g84,g85)
    c: Coincident(g85,g86)
    c: Coincident(g86,g87)
    c: Coincident(g87,g88)
    c: Coincident(g88,g89)
    c: Coincident(g90,g91)
    c: Coincident(g91,g92)
    c: Coincident(g92,g93)
    c: Coincident(g93,g94)
    c: Coincident(g94,g95)
    c: Coincident(g95,g96)
    c: Coincident(g96,g97)
    c: Coincident(g97,g98)
    c: Coincident(g98,g99)
    c: Coincident(g99,g100)
    c: Coincident(g100,g101)
FEATURE [Sketcher::SketchObject] Sketch053
  ArcFitTolerance = 1e-06
  AttachmentSupport = -> [Hole010]
  ExternalGeometry = -> [Sketch052]
  FullyConstrained = true
  MakeInternals = false
  MapMode = 5
  Placement = pos=(-16.5,0,0) rot=(0.707107,0,-0.707107;3.14159rad)
  sketch-geometry (4):
    g0: Circle CenterX=-1.15 CenterY=77.0838 CenterZ=0 NormalX=0 NormalY=0 NormalZ=1 AngleXU=0 Radius=1.75
    g1: Circle CenterX=-1.15 CenterY=35.6538 CenterZ=0 NormalX=0 NormalY=0 NormalZ=1 AngleXU=0 Radius=1.75
    g2: Circle CenterX=-1.15 CenterY=-35.5538 CenterZ=0 NormalX=0 NormalY=0 NormalZ=1 AngleXU=0 Radius=1.75
    g3: Circle CenterX=-1.15 CenterY=-76.9519 CenterZ=0 NormalX=0 NormalY=0 NormalZ=1 AngleXU=0 Radius=1.75
  constraints (8):
    c: Coincident(g0,g-3)
    c: PointOnObject(g-3,g0)
    c: Coincident(g1,g-4)
    c: PointOnObject(g-4,g1)
    c: Coincident(g2,g-5)
    c: PointOnObject(g-5,g2)
    c: Coincident(g3,g-6)
    c: PointOnObject(g-6,g3)
FEATURE [PartDesign::Hole] Hole011
  BaseFeature = -> Hole010
  CustomThreadClearance = 0
  Depth = 367.043
  DepthType = 1
  Diameter = 3.4
  DrillForDepth = false
  DrillPoint = 1
  DrillPointAngle = 118
  HoleCutCountersinkAngle = 90
  HoleCutCustomValues = false
  HoleCutDepth = 0
  HoleCutDiameter = 6.1
  HoleCutType = 0
  ModelThread = false
  Placement = pos=(0,0,0) rot=(1,0,0;1.5708rad)
  Profile = -> Sketch053
  Refine = true
  Suppressed = false
  Tapered = false
  TaperedAngle = 90
  ThreadClass = 0
  ThreadDepth = 367.043
  ThreadDepthType = 0
  ThreadDirection = 0
  ThreadFit = 0
  ThreadSize = 9
  ThreadType = 1
  Threaded = false
  UseCustomThreadClearance = false
FEATURE [PartDesign::Fillet] Fillet003
  Base = -> Hole011 [Edge9,Edge8]
  BaseFeature = -> Hole011
  Placement = pos=(0,0,0) rot=(1,0,0;1.5708rad)
  Radius = 7
  Refine = true
  SupportTransform = false
  Suppressed = false
  UseAllEdges = false
FEATURE [Sketcher::SketchObject] Sketch054
  ArcFitTolerance = 1e-06
  AttachmentSupport = -> [Fillet003]
  ExternalGeometry = -> [Fillet003,Sketch052]
  FullyConstrained = true
  MakeInternals = false
  MapMode = 5
  Placement = pos=(-16.5,0,0) rot=(0.707107,0,-0.707107;3.14159rad)
  sketch-geometry (14):
    g0: ArcOfCircle CenterX=-1.15 CenterY=77.0838 CenterZ=0 NormalX=0 NormalY=0 NormalZ=1 AngleXU=0 Radius=5.98816 StartAngle=4.93602 EndAngle=7.63036
    g1: LineSegment StartX=6 StartY=90 StartZ=0 EndX=0.17798 EndY=90 EndZ=0
    g2: LineSegment StartX=0.17798 StartY=90 StartZ=0 EndX=0.17798 EndY=82.9228 EndZ=0
    g3: GeomPoint X=0.67798 Y=90 Z=0
    g4: GeomPoint X=4.83816 Y=77.0838 Z=0
    g5: LineSegment StartX=0.17798 StartY=71.2447 StartZ=0 EndX=0.17798 EndY=41.4928 EndZ=0
    g6: ArcOfCircle CenterX=-1.15 CenterY=35.6538 CenterZ=0 NormalX=0 NormalY=0 NormalZ=1 AngleXU=0 Radius=5.98816 StartAngle=4.93602 EndAngle=7.63036
    g7: ArcOfCircle CenterX=-1.15 CenterY=-35.5538 CenterZ=0 NormalX=0 NormalY=0 NormalZ=1 AngleXU=0 Radius=5.98816 StartAngle=4.93602 EndAngle=7.63036
    g8: ArcOfCircle CenterX=-1.15 CenterY=-76.9519 CenterZ=0 NormalX=0 NormalY=0 NormalZ=1 AngleXU=0 Radius=5.98816 StartAngle=4.93602 EndAngle=7.63036
    g9: LineSegment StartX=0.17798 StartY=29.8147 StartZ=0 EndX=0.17798 EndY=-29.7147 EndZ=0
    g10: LineSegment StartX=0.17798 StartY=-41.3928 StartZ=0 EndX=0.17798 EndY=-71.1129 EndZ=0
    g11: LineSegment StartX=0.17798 StartY=-82.791 StartZ=0 EndX=0.17798 EndY=-90 EndZ=0
    g12: LineSegment StartX=0.17798 StartY=-90 StartZ=0 EndX=6 EndY=-90 EndZ=0
    g13: LineSegment StartX=6 StartY=-90 StartZ=0 EndX=6 EndY=90 EndZ=0
  constraints (38):
    c: Coincident(g0,g-13)
    c: Coincident(g-3,g1)
    c: PointOnObject(g1,g-3)
    c: Coincident(g1,g2)
    c: Vertical(g2)
    c: Coincident(g2,g0)
    c: PointOnObject(g3,g1)
    c: PointOnObject(g3,g-4)
    c: Distance(g1,g3) = 0.5
    c: PointOnObject(g4,g0)
    c: Horizontal(g0,g4)
    c: Distance(g4,g-14) = 0.5
    c: Coincident(g5,g0)
    c: Vertical(g5)
    c: Vertical(g0,g0)
    c: Coincident(g6,g-11)
    c: Coincident(g7,g-9)
    c: Coincident(g8,g-10)
    c: Coincident(g6,g5)
    c: Equal(g6,g0)
    c: Vertical(g5,g6)
    c: Coincident(g9,g6)
    c: Coincident(g9,g7)
    c: Vertical(g9)
    c: Equal(g7,g6)
    c: Vertical(g7,g7)
    c: Coincident(g10,g7)
    c: Coincident(g10,g8)
    c: Vertical(g10)
    c: Vertical(g8,g8)
    c: Equal(g8,g7)
    c: Coincident(g11,g8)
    c: PointOnObject(g11,g-5)
    c: Vertical(g11)
    c: Coincident(g12,g11)
    c: Coincident(g12,g-5)
    c: Coincident(g13,g12)
    c: Coincident(g13,g1)
FEATURE [PartDesign::Pocket] Pocket  label="TrimOffBelowWheels"
  BaseFeature = -> Fillet003
  Direction = (1,0,2e-16)
  Length = 5
  Length2 = 5
  Placement = pos=(0,0,0) rot=(1,0,0;1.5708rad)
  Profile = -> Sketch054
  ReferenceAxis = -> Sketch054 [N_Axis]
  Refine = true
  Suppressed = false
  Type = 1
FEATURE [Sketcher::SketchObject] Sketch064
  ArcFitTolerance = 1e-06
  AttachmentSupport = -> [Pocket]
  ExternalGeometry = -> [Pocket]
  FullyConstrained = true
  MakeInternals = false
  MapMode = 5
  Placement = pos=(-13.5,0,0) rot=(0.707107,0,0.707107;3.14159rad)
  sketch-geometry (28):
    g0: LineSegment StartX=4.6141 StartY=77.0838 StartZ=0 EndX=2.88205 EndY=80.0838 EndZ=0
    g1: LineSegment StartX=2.88205 StartY=80.0838 StartZ=0 EndX=-0.582053 EndY=80.0838 EndZ=0
    g2: LineSegment StartX=-0.582053 StartY=80.0838 StartZ=0 EndX=-2.3141 EndY=77.0838 EndZ=0
    g3: LineSegment StartX=-2.3141 StartY=77.0838 StartZ=0 EndX=-0.582053 EndY=74.0838 EndZ=0
    g4: LineSegment StartX=-0.582053 StartY=74.0838 StartZ=0 EndX=2.88205 EndY=74.0838 EndZ=0
    g5: LineSegment StartX=2.88205 StartY=74.0838 StartZ=0 EndX=4.6141 EndY=77.0838 EndZ=0
    g6: Circle [constr] CenterX=1.15 CenterY=77.0838 CenterZ=0 NormalX=0 NormalY=0 NormalZ=1 AngleXU=0 Radius=3.4641
    g7: LineSegment StartX=4.6141 StartY=35.6538 StartZ=0 EndX=2.88205 EndY=38.6538 EndZ=0
    g8: LineSegment StartX=2.88205 StartY=38.6538 StartZ=0 EndX=-0.582053 EndY=38.6538 EndZ=0
    g9: LineSegment StartX=-0.582053 StartY=38.6538 StartZ=0 EndX=-2.3141 EndY=35.6538 EndZ=0
    g10: LineSegment StartX=-2.3141 StartY=35.6538 StartZ=0 EndX=-0.582053 EndY=32.6538 EndZ=0
    g11: LineSegment StartX=-0.582053 StartY=32.6538 StartZ=0 EndX=2.88205 EndY=32.6538 EndZ=0
    g12: LineSegment StartX=2.88205 StartY=32.6538 StartZ=0 EndX=4.6141 EndY=35.6538 EndZ=0
    g13: Circle [constr] CenterX=1.15 CenterY=35.6538 CenterZ=0 NormalX=0 NormalY=0 NormalZ=1 AngleXU=0 Radius=3.4641
    g14: LineSegment StartX=4.6141 StartY=-35.5538 StartZ=0 EndX=2.88205 EndY=-32.5538 EndZ=0
    g15: LineSegment StartX=2.88205 StartY=-32.5538 StartZ=0 EndX=-0.582053 EndY=-32.5538 EndZ=0
    g16: LineSegment StartX=-0.582053 StartY=-32.5538 StartZ=0 EndX=-2.3141 EndY=-35.5538 EndZ=0
    g17: LineSegment StartX=-2.3141 StartY=-35.5538 StartZ=0 EndX=-0.582053 EndY=-38.5538 EndZ=0
    g18: LineSegment StartX=-0.582053 StartY=-38.5538 StartZ=0 EndX=2.88205 EndY=-38.5538 EndZ=0
    g19: LineSegment StartX=2.88205 StartY=-38.5538 StartZ=0 EndX=4.6141 EndY=-35.5538 EndZ=0
    g20: Circle [constr] CenterX=1.15 CenterY=-35.5538 CenterZ=0 NormalX=0 NormalY=0 NormalZ=1 AngleXU=0 Radius=3.4641
    g21: LineSegment StartX=4.6141 StartY=-76.9519 StartZ=0 EndX=2.88205 EndY=-73.9519 EndZ=0
    g22: LineSegment StartX=2.88205 StartY=-73.9519 StartZ=0 EndX=-0.582053 EndY=-73.9519 EndZ=0
    g23: LineSegment StartX=-0.582053 StartY=-73.9519 StartZ=0 EndX=-2.3141 EndY=-76.9519 EndZ=0
    g24: LineSegment StartX=-2.3141 StartY=-76.9519 StartZ=0 EndX=-0.582053 EndY=-79.9519 EndZ=0
    g25: LineSegment StartX=-0.582053 StartY=-79.9519 StartZ=0 EndX=2.88205 EndY=-79.9519 EndZ=0
    g26: LineSegment StartX=2.88205 StartY=-79.9519 StartZ=0 EndX=4.6141 EndY=-76.9519 EndZ=0
    g27: Circle [constr] CenterX=1.15 CenterY=-76.9519 CenterZ=0 NormalX=0 NormalY=0 NormalZ=1 AngleXU=0 Radius=3.4641
  constraints (64):
    c: Coincident(g0,g1)
    c: Coincident(g1,g2)
    c: Coincident(g2,g3)
    c: Coincident(g3,g4)
    c: Coincident(g4,g5)
    c: Coincident(g5,g0)
    c: Equal(g0, g1-g5) x5
    c: PointOnObject(g0,g6)
    c: PointOnObject(g1,g6)
    c: PointOnObject(g2,g6)
    c: PointOnObject(g3,g6)
    c: PointOnObject(g4,g6)
    c: PointOnObject(g5,g6)
    c: Coincident(g6,g-3)
    c: Horizontal(g1)
    c: Distance(g4,g1) = 6
    c: Coincident(g7,g8)
    c: Coincident(g8,g9)
    c: Coincident(g9,g10)
    c: Coincident(g10,g11)
    c: Coincident(g11,g12)
    c: Coincident(g12,g7)
    c: Equal(g7, g8-g12) x5
    c: PointOnObject(g7,g13)
    c: PointOnObject(g8,g13)
    c: PointOnObject(g9,g13)
    c: PointOnObject(g10,g13)
    c: PointOnObject(g11,g13)
    c: PointOnObject(g12,g13)
    c: Coincident(g13,g-4)
    c: Coincident(g14,g15)
    c: Coincident(g15,g16)
    c: Coincident(g16,g17)
    c: Coincident(g17,g18)
    c: Coincident(g18,g19)
    c: Coincident(g19,g14)
    c: Equal(g14, g15-g19) x5
    c: PointOnObject(g14,g20)
    c: PointOnObject(g15,g20)
    c: PointOnObject(g16,g20)
    c: PointOnObject(g17,g20)
    c: PointOnObject(g18,g20)
    c: PointOnObject(g19,g20)
    c: Coincident(g20,g-5)
    c: Coincident(g21,g22)
    c: Coincident(g22,g23)
    c: Coincident(g23,g24)
    c: Coincident(g24,g25)
    c: Coincident(g25,g26)
    c: Coincident(g26,g21)
    c: Equal(g21, g22-g26) x5
    c: PointOnObject(g21,g27)
    c: PointOnObject(g22,g27)
    c: PointOnObject(g23,g27)
    c: PointOnObject(g24,g27)
    c: PointOnObject(g25,g27)
    c: PointOnObject(g26,g27)
    c: Coincident(g27,g-6)
    c: Horizontal(g22)
    c: Equal(g22,g15)
    c: Horizontal(g15)
    c: Equal(g15,g8)
    c: Horizontal(g8)
    c: Equal(g8,g1)
FEATURE [PartDesign::Pocket] Pocket022  label="HexNutHole001"
  BaseFeature = -> Pocket
  Direction = (-1,0,2e-16)
  Length = 1
  Length2 = 5
  Placement = pos=(0,0,0) rot=(1,0,0;1.5708rad)
  Profile = -> Sketch064
  ReferenceAxis = -> Sketch064 [N_Axis]
  Refine = true
  Suppressed = false
  Type = 0
FEATURE [PartDesign::Body] Body003  label="TramCarriage"
  AllowCompound = false
  Group = -> [Binder003,Binder004,Sketch008,Pad004,Binder005,Binder006,Sketch010,Sketch052,Hole010,Sketch053,Hole011,Fillet003,Sketch054,Pocket,Sketch064,Pocket022]
  Origin = -> Origin003
  Tip = -> Pocket022
COMPONENT P14 — recipe-attached ("TramPlaceholder001", modeled in this document).
Construction recipe (the document's own serialized feature program — sketch geometry with constraints, then the solid features built on it; lengths are millimeters unless a unit is written):

FEATURE [Sketcher::SketchObject] Sketch066
  ArcFitTolerance = 1e-06
  FullyConstrained = false
  MakeInternals = false
  sketch-geometry (78):
    g0: BSplineCurve PolesCount=4 KnotsCount=2 Degree=3 IsPeriodic=0
    g1: BSplineCurve PolesCount=4 KnotsCount=2 Degree=3 IsPeriodic=0
    g2: BSplineCurve PolesCount=4 KnotsCount=2 Degree=3 IsPeriodic=0
    g3: BSplineCurve PolesCount=2 KnotsCount=2 Degree=1 IsPeriodic=0
    g4: BSplineCurve PolesCount=2 KnotsCount=2 Degree=1 IsPeriodic=0
    g5: BSplineCurve PolesCount=2 KnotsCount=2 Degree=1 IsPeriodic=0
    g6: BSplineCurve PolesCount=2 KnotsCount=2 Degree=1 IsPeriodic=0
    g7: BSplineCurve PolesCount=2 KnotsCount=2 Degree=1 IsPeriodic=0
    g8: BSplineCurve PolesCount=4 KnotsCount=2 Degree=3 IsPeriodic=0
    g9: BSplineCurve PolesCount=4 KnotsCount=2 Degree=3 IsPeriodic=0
    g10: BSplineCurve PolesCount=2 KnotsCount=2 Degree=1 IsPeriodic=0
    g11: BSplineCurve PolesCount=4 KnotsCount=2 Degree=3 IsPeriodic=0
    g12: BSplineCurve PolesCount=4 KnotsCount=2 Degree=3 IsPeriodic=0
    g13: BSplineCurve PolesCount=2 KnotsCount=2 Degree=1 IsPeriodic=0
    g14: BSplineCurve PolesCount=2 KnotsCount=2 Degree=1 IsPeriodic=0
    g15: BSplineCurve PolesCount=4 KnotsCount=2 Degree=3 IsPeriodic=0
    g16: BSplineCurve PolesCount=4 KnotsCount=2 Degree=3 IsPeriodic=0
    g17: BSplineCurve PolesCount=2 KnotsCount=2 Degree=1 IsPeriodic=0
    g18: BSplineCurve PolesCount=4 KnotsCount=2 Degree=3 IsPeriodic=0
    g19: BSplineCurve PolesCount=4 KnotsCount=2 Degree=3 IsPeriodic=0
    g20: BSplineCurve PolesCount=2 KnotsCount=2 Degree=1 IsPeriodic=0
    g21: BSplineCurve PolesCount=2 KnotsCount=2 Degree=1 IsPeriodic=0
    g22: BSplineCurve PolesCount=2 KnotsCount=2 Degree=1 IsPeriodic=0
    g23: BSplineCurve PolesCount=2 KnotsCount=2 Degree=1 IsPeriodic=0
    g24: BSplineCurve PolesCount=2 KnotsCount=2 Degree=1 IsPeriodic=0
    g25: BSplineCurve PolesCount=2 KnotsCount=2 Degree=1 IsPeriodic=0
    g26: BSplineCurve PolesCount=2 KnotsCount=2 Degree=1 IsPeriodic=0
    g27: BSplineCurve PolesCount=2 KnotsCount=2 Degree=1 IsPeriodic=0
    g28: BSplineCurve PolesCount=2 KnotsCount=2 Degree=1 IsPeriodic=0
    g29: BSplineCurve PolesCount=4 KnotsCount=2 Degree=3 IsPeriodic=0
    g30: BSplineCurve PolesCount=4 KnotsCount=2 Degree=3 IsPeriodic=0
    g31: BSplineCurve PolesCount=2 KnotsCount=2 Degree=1 IsPeriodic=0
    g32: BSplineCurve PolesCount=4 KnotsCount=2 Degree=3 IsPeriodic=0
    g33: BSplineCurve PolesCount=4 KnotsCount=2 Degree=3 IsPeriodic=0
    g34: BSplineCurve PolesCount=2 KnotsCount=2 Degree=1 IsPeriodic=0
    g35: BSplineCurve PolesCount=2 KnotsCount=2 Degree=1 IsPeriodic=0
    g36: BSplineCurve PolesCount=4 KnotsCount=2 Degree=3 IsPeriodic=0
    g37: BSplineCurve PolesCount=4 KnotsCount=2 Degree=3 IsPeriodic=0
    g38: BSplineCurve PolesCount=2 KnotsCount=2 Degree=1 IsPeriodic=0
    g39: BSplineCurve PolesCount=4 KnotsCount=2 Degree=3 IsPeriodic=0
    g40: BSplineCurve PolesCount=4 KnotsCount=2 Degree=3 IsPeriodic=0
    g41: BSplineCurve PolesCount=2 KnotsCount=2 Degree=1 IsPeriodic=0
    g42: BSplineCurve PolesCount=2 KnotsCount=2 Degree=1 IsPeriodic=0
    g43: BSplineCurve PolesCount=2 KnotsCount=2 Degree=1 IsPeriodic=0
    g44: BSplineCurve PolesCount=2 KnotsCount=2 Degree=1 IsPeriodic=0
    g45: BSplineCurve PolesCount=2 KnotsCount=2 Degree=1 IsPeriodic=0
    g46: BSplineCurve PolesCount=4 KnotsCount=2 Degree=3 IsPeriodic=0
    g47: BSplineCurve PolesCount=4 KnotsCount=2 Degree=3 IsPeriodic=0
    g48: BSplineCurve PolesCount=4 KnotsCount=2 Degree=3 IsPeriodic=0
    g49: BSplineCurve PolesCount=4 KnotsCount=2 Degree=3 IsPeriodic=0
    g50: BSplineCurve PolesCount=4 KnotsCount=2 Degree=3 IsPeriodic=0
    g51: BSplineCurve PolesCount=2 KnotsCount=2 Degree=1 IsPeriodic=0
    g52: BSplineCurve PolesCount=4 KnotsCount=2 Degree=3 IsPeriodic=0
    g53: BSplineCurve PolesCount=2 KnotsCount=2 Degree=1 IsPeriodic=0
    g54: BSplineCurve PolesCount=4 KnotsCount=2 Degree=3 IsPeriodic=0
    g55: BSplineCurve PolesCount=2 KnotsCount=2 Degree=1 IsPeriodic=0
    g56: BSplineCurve PolesCount=2 KnotsCount=2 Degree=1 IsPeriodic=0
    g57: BSplineCurve PolesCount=2 KnotsCount=2 Degree=1 IsPeriodic=0
    g58: BSplineCurve PolesCount=2 KnotsCount=2 Degree=1 IsPeriodic=0
    g59: BSplineCurve PolesCount=2 KnotsCount=2 Degree=1 IsPeriodic=0
    g60: BSplineCurve PolesCount=2 KnotsCount=2 Degree=1 IsPeriodic=0
    g61: BSplineCurve PolesCount=2 KnotsCount=2 Degree=1 IsPeriodic=0
    g62: BSplineCurve PolesCount=2 KnotsCount=2 Degree=1 IsPeriodic=0
    g63: BSplineCurve PolesCount=2 KnotsCount=2 Degree=1 IsPeriodic=0
    g64: BSplineCurve PolesCount=4 KnotsCount=2 Degree=3 IsPeriodic=0
    g65: BSplineCurve PolesCount=2 KnotsCount=2 Degree=1 IsPeriodic=0
    g66: BSplineCurve PolesCount=4 KnotsCount=2 Degree=3 IsPeriodic=0
    g67: BSplineCurve PolesCount=2 KnotsCount=2 Degree=1 IsPeriodic=0
    g68: BSplineCurve PolesCount=4 KnotsCount=2 Degree=3 IsPeriodic=0
    g69: BSplineCurve PolesCount=4 KnotsCount=2 Degree=3 IsPeriodic=0
    g70: BSplineCurve [constr] PolesCount=2 KnotsCount=2 Degree=1 IsPeriodic=0
    g71: BSplineCurve [constr] PolesCount=2 KnotsCount=2 Degree=1 IsPeriodic=0
    g72: BSplineCurve [constr] PolesCount=2 KnotsCount=2 Degree=1 IsPeriodic=0
    g73: BSplineCurve [constr] PolesCount=2 KnotsCount=2 Degree=1 IsPeriodic=0
    g74: Circle CenterX=44.7617 CenterY=-141.918 CenterZ=0 NormalX=0 NormalY=0 NormalZ=1 AngleXU=0 Radius=1.75
    g75: Circle CenterX=86.1598 CenterY=-141.918 CenterZ=0 NormalX=0 NormalY=0 NormalZ=1 AngleXU=0 Radius=1.75
    g76: Circle CenterX=157.367 CenterY=-141.918 CenterZ=0 NormalX=0 NormalY=0 NormalZ=1 AngleXU=0 Radius=1.75
    g77: Circle CenterX=198.797 CenterY=-141.918 CenterZ=0 NormalX=0 NormalY=0 NormalZ=1 AngleXU=0 Radius=1.75
  constraints (78):
    c: Coincident(g0,g1)
    c: Coincident(g1,g2)
    c: Coincident(g2,g3)
    c: Coincident(g3,g4)
    c: Coincident(g4,g5)
    c: Coincident(g5,g6)
    c: Coincident(g6,g7)
    c: Coincident(g7,g8)
    c: Coincident(g8,g9)
    c: Coincident(g9,g10)
    c: Coincident(g10,g11)
    c: Coincident(g11,g12)
    c: Coincident(g12,g13)
    c: Coincident(g13,g14)
    c: Coincident(g14,g15)
    c: Coincident(g15,g16)
    c: Coincident(g16,g17)
    c: Coincident(g17,g18)
    c: Coincident(g18,g19)
    c: Coincident(g19,g20)
    c: Coincident(g20,g21)
    c: Coincident(g21,g22)
    c: Coincident(g22,g23)
    c: Coincident(g23,g24)
    c: Coincident(g24,g25)
    c: Coincident(g25,g26)
    c: Coincident(g26,g27)
    c: Coincident(g27,g28)
    c: Coincident(g28,g29)
    c: Coincident(g29,g30)
    c: Coincident(g30,g31)
    c: Coincident(g31,g32)
    c: Coincident(g32,g33)
    c: Coincident(g33,g34)
    c: Coincident(g34,g35)
    c: Coincident(g35,g36)
    c: Coincident(g36,g37)
    c: Coincident(g37,g38)
    c: Coincident(g38,g39)
    c: Coincident(g39,g40)
    c: Coincident(g40,g41)
    c: Coincident(g41,g42)
    c: Coincident(g42,g43)
    c: Coincident(g43,g44)
    c: Coincident(g44,g45)
    c: Coincident(g45,g46)
    c: Coincident(g46,g47)
    c: Coincident(g47,g48)
    c: Coincident(g48,g49)
    c: Coincident(g49,g50)
    c: Coincident(g50,g51)
    c: Coincident(g51,g52)
    c: Coincident(g52,g53)
    c: Coincident(g53,g54)
    c: Coincident(g54,g55)
    c: Coincident(g55,g56)
    c: Coincident(g56,g57)
    c: Coincident(g57,g58)
    c: Coincident(g58,g59)
    c: Coincident(g59,g60)
    c: Coincident(g60,g61)
    c: Coincident(g61,g62)
    c: Coincident(g62,g63)
    c: Coincident(g63,g64)
    c: Coincident(g64,g65)
    c: Coincident(g65,g66)
    c: Coincident(g66,g67)
    c: Coincident(g67,g68)
    c: Coincident(g68,g69)
    c: Coincident(g69,g0)
    c: Coincident(g74,g70)
    c: PointOnObject(g70,g74)
    c: Coincident(g75,g71)
    c: PointOnObject(g71,g75)
    c: Coincident(g76,g72)
    c: PointOnObject(g72,g76)
    c: Coincident(g77,g73)
    c: PointOnObject(g73,g77)
FEATURE [PartDesign::Pad] Pad025
  Direction = (0,0,1)
  Length = 5
  Length2 = 10
  Profile = -> Sketch066
  ReferenceAxis = -> Sketch066 [N_Axis]
  Refine = true
  Suppressed = false
  Type = 0
FEATURE [PartDesign::Body] Body012  label="TramPlaceholder"
  AllowCompound = false
  Group = -> [Sketch066,Pad025]
  Origin = -> Origin014
  Tip = -> Pad025
PROVENANCE & LICENSES
A FreeCAD (.FCStd) document from a public repository crawl; recipes are the document's own serialized feature recipes (and, for linked parts, companion documents' recipes).
License: gpl-3.0.
